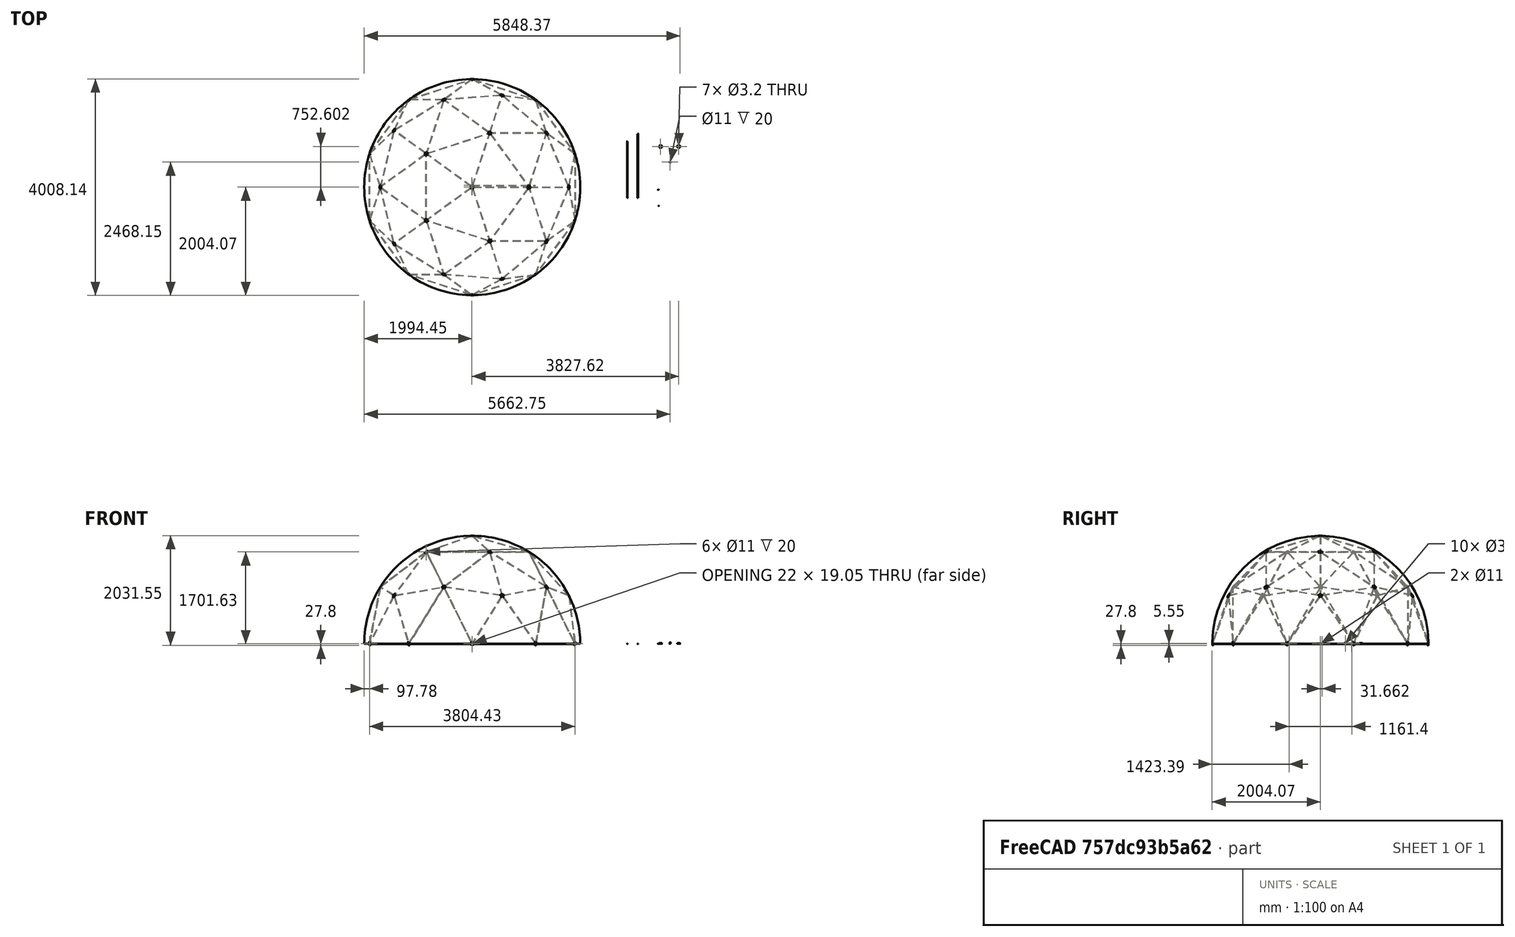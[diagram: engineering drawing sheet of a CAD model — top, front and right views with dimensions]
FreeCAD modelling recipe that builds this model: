
FCSTD DOCUMENT  (FreeCAD 0.19R24291 (Git))
Label: 02-domo-3D
License: All rights reserved
LicenseURL: http://en.wikipedia.org/wiki/All_rights_reserved
objects: Part::Feature×235, Part::Part2DObjectPython×138, App::DocumentObjectGroup×21, App::Annotation×18, Part::Mirroring×7, App::FeaturePython×4, Part::Sphere×1, Part::Cylinder×1
note: 382 computed .brp shape members not serialized (recipe doc carries the construction recipe); baked Part::Feature solids carry a one-line shape summary decoded from their .brp

FEATURE [Part::Part2DObjectPython] Line  # Draft 2D object (typed FeaturePython)
  ChamferSize = 0
  Closed = false
  End = (-1902.16,617.998,0)
  FilletRadius = 0
  Length = 1236.1
  MakeFace = true
  MapMode = 5
  Placement = pos=(-1154.86,1595.54,0) rot=(0,0,-1;0.628319rad)
  Points = (2) [(-30,6,0),(-30,-1230.1,0)]
  Start = (-1175.6,1618.02,0)
  Subdivisions = 0
FEATURE [Part::Part2DObjectPython] Line003  # Draft 2D object (typed FeaturePython)
  ChamferSize = 0
  Closed = false
  End = (-1175.6,1618.02,0)
  FilletRadius = 0
  Length = 1236.1
  MakeFace = true
  MapMode = 5
  Placement = pos=(3.56417,1969.61,0) rot=(0,0,-1;1.25664rad)
  Points = (2) [(-30,6,0),(-30,-1230.1,0)]
  Start = (3.57132e-11,2000,0)
  Subdivisions = 0
FEATURE [Part::Mirroring] Part__Mirroring  label="Line (Mirror #1)"
  Base = (0,0,0)
  Normal = (1,0,0)
  Source = -> Line
FEATURE [Part::Mirroring] Part__Mirroring001  label="Line003 (Mirror #2)"
  Base = (0,0,0)
  Normal = (1,0,0)
  Source = -> Line003
FEATURE [Part::Mirroring] Part__Mirroring002  label="Line (Mirror #3)"
  Base = (0,0,0)
  Normal = (0,1,0)
  Source = -> Line
FEATURE [Part::Mirroring] Part__Mirroring003  label="Line003 (Mirror #4)"
  Base = (0,0,0)
  Normal = (0,1,0)
  Source = -> Line003
FEATURE [Part::Mirroring] Part__Mirroring004  label="Line (Mirror #5)"
  Base = (0,0,0)
  Normal = (0,1,0)
  Source = -> Part__Mirroring
FEATURE [Part::Mirroring] Part__Mirroring005  label="Line003 (Mirror #6)"
  Base = (0,0,0)
  Normal = (0,1,0)
  Source = -> Part__Mirroring001
FEATURE [Part::Part2DObjectPython] Line006  # Draft 2D object (typed FeaturePython)
  ChamferSize = 0
  Closed = false
  End = (-1902.16,-617.998,0)
  FilletRadius = 0
  Length = 1236
  MakeFace = true
  MapMode = 5
  Points = (2) [(-1902.16,617.998,0),(-1902.16,-617.998,0)]
  Start = (-1902.16,617.998,0)
  Subdivisions = 0
FEATURE [Part::Sphere] Sphere
  Angle1 = 0
  Angle2 = 90
  Angle3 = 360
  AttacherType = Attacher::AttachEngine3D
  Radius = 2000
FEATURE [Part::Part2DObjectPython] Line014  # Draft 2D object (typed FeaturePython)
  ChamferSize = 0
  Closed = false
  End = (1902.16,3e-10,0)
  FilletRadius = 0
  Length = 1902.16
  MakeFace = true
  MapMode = 5
  Points = (2) [(-1.99975e-10,3.00133e-10,0),(1902.16,3.0025e-10,0)]
  Start = (0,0,0)
  Subdivisions = 0
FEATURE [Part::Part2DObjectPython] Line015  # Draft 2D object (typed FeaturePython)
  ChamferSize = 0
  Closed = false
  End = (1902.16,3e-10,0)
  FilletRadius = 0
  Length = 1902.16
  MakeFace = true
  MapMode = 5
  Points = (2) [(-1.99975e-10,3.00133e-10,0),(1902.16,3.0025e-10,0)]
  Start = (0,0,0)
  Subdivisions = 0
FEATURE [Part::Part2DObjectPython] Line016  # Draft 2D object (typed FeaturePython)
  ChamferSize = 0
  Closed = false
  End = (587.785,1809.02,0)
  FilletRadius = 0
  Length = 1902.11
  MakeFace = true
  MapMode = 5
  Points = (2) [(-1.99975e-10,3.00133e-10,0),(587.785,1809.02,0)]
  Start = (0,0,0)
  Subdivisions = 0
FEATURE [Part::Part2DObjectPython] Line017  # Draft 2D object (typed FeaturePython)
  ChamferSize = 0
  Closed = false
  End = (-1538.86,1118.05,0)
  FilletRadius = 0
  Length = 1902.13
  MakeFace = true
  MapMode = 5
  Points = (2) [(-1.99975e-10,3.00133e-10,0),(-1538.86,1118.05,0)]
  Start = (0,0,0)
  Subdivisions = 0
FEATURE [Part::Part2DObjectPython] Line018  # Draft 2D object (typed FeaturePython)
  ChamferSize = 0
  Closed = false
  End = (-1538.86,-1118.05,0)
  FilletRadius = 0
  Length = 1902.13
  MakeFace = true
  MapMode = 5
  Points = (2) [(-1.99975e-10,3.00133e-10,0),(-1538.86,-1118.05,0)]
  Start = (0,0,0)
  Subdivisions = 0
FEATURE [Part::Part2DObjectPython] Line019  # Draft 2D object (typed FeaturePython)
  ChamferSize = 0
  Closed = false
  End = (-577.454,-703.099,0)
  FilletRadius = 0
  Length = 1093.1
  MakeFace = true
  MapMode = 5
  Placement = pos=(1075.61,-2380.95,0) rot=(0,0,-1;0.581932rad)
  Points = (2) [(-2300,-600,0),(-2303.19,493.095,0)]
  Start = (-1175.6,-1618.02,0)
  Subdivisions = 0
FEATURE [Part::Part2DObjectPython] Line022  # Draft 2D object (typed FeaturePython)
  ChamferSize = 0
  Closed = false
  End = (587.8,-1809.01,0)
  FilletRadius = 0
  Length = 1902.11
  MakeFace = true
  MapMode = 5
  Points = (2) [(-1.99975e-10,3.00133e-10,0),(587.8,-1809.01,0)]
  Start = (0,0,0)
  Subdivisions = 0
FEATURE [Part::Part2DObjectPython] Line023  # Draft 2D object (typed FeaturePython)
  ChamferSize = 0
  Closed = false
  End = (0,0,2000)
  FilletRadius = 0
  Length = 2000
  MakeFace = true
  MapMode = 5
  Points = (2) [(-1.99975e-10,3.00133e-10,0),(1.22465e-13,-2.99952e-29,2000)]
  Start = (0,0,0)
  Subdivisions = 0
FEATURE [Part::Part2DObjectPython] DWire001  # Draft 2D object (typed FeaturePython)
  ChamferSize = 0
  Closed = true
  End = (1902.16,617.998,0)
  FilletRadius = 0
  Length = 3422.2
  MakeFace = true
  MapMode = 5
  Points = (3) [(1902.16,-617.998,0),(1788.83,-9.64734e-10,894.484),(1902.16,617.998,0)]
  Start = (1902.16,-617.998,0)
  Subdivisions = 0
FEATURE [Part::Part2DObjectPython] DWire  # Draft 2D object (typed FeaturePython)
  ChamferSize = 0
  Closed = true
  End = (587.785,1809.02,0)
  FilletRadius = 0
  Length = 6662.19
  MakeFace = true
  MapMode = 5
  Points = (3) [(1.22465e-13,0,2000),(-1.99975e-10,3.00133e-10,0),(587.785,1809.02,0)]
  Start = (0,0,2000)
  Subdivisions = 0
FEATURE [Part::Mirroring] Part__Mirroring006  label="DWire003 (Mirror #7)"
  Base = (0,0,0)
  Normal = (0,1,0)
FEATURE [Part::Part2DObjectPython] Arc  # Draft 2D object (typed FeaturePython)
  FirstAngle = 56.8247
  LastAngle = 105.817
  MakeFace = true
  MapMode = 5
  Placement = pos=(-1175.6,-1618.02,0) rot=(0,0,1;0rad)
  Radius = 1093.1
FEATURE [Part::Part2DObjectPython] Line026  # Draft 2D object (typed FeaturePython)
  ChamferSize = 0
  Closed = false
  End = (-1902.16,-617.998,0)
  FilletRadius = 0
  Length = 1093.15
  MakeFace = true
  MapMode = 5
  Points = (2) [(-809.424,-588.081,0),(-1902.16,-617.998,0)]
  Start = (-809.424,-588.081,0)
  Subdivisions = 0
FEATURE [Part::Part2DObjectPython] DWire004  # Draft 2D object (typed FeaturePython)
  ChamferSize = 0
  Closed = true
  End = (-1538.86,-1118.05,0)
  FilletRadius = 0
  Length = 6662.22
  MakeFace = true
  MapMode = 5
  Points = (3) [(1.22465e-13,0,2000),(-1.99975e-10,3.00133e-10,0),(-1538.86,-1118.05,0)]
  Start = (0,0,2000)
  Subdivisions = 0
FEATURE [Part::Part2DObjectPython] DWire005  # Draft 2D object (typed FeaturePython)
  ChamferSize = 0
  Closed = true
  End = (-1175.6,-1618.02,0)
  FilletRadius = 0
  Length = 3422.35
  MakeFace = true
  MapMode = 5
  Points = (3) [(-1902.16,-617.998,0),(-1447.19,-1051.45,894.481),(-1175.6,-1618.02,0)]
  Start = (-1902.16,-617.998,0)
  Subdivisions = 0
FEATURE [Part::Part2DObjectPython] Line027  # Draft 2D object (typed FeaturePython)
  ChamferSize = 0
  Closed = false
  End = (-878.683,234.127,0)
  FilletRadius = 0
  Length = 1093.1
  MakeFace = true
  MapMode = 5
  Placement = pos=(-2154.97,-1745.49,0) rot=(0,0,-1;1.93254rad)
  Points = (2) [(-2300,-600,0),(-2303.19,493.095,0)]
  Start = (-1902.16,617.998,0)
  Subdivisions = 0
FEATURE [Part::Part2DObjectPython] Arc003  # Draft 2D object (typed FeaturePython)
  FirstAngle = -20.5593
  LastAngle = 28.7005
  MakeFace = true
  MapMode = 5
  Placement = pos=(-1902.16,617.998,0) rot=(0,0,1;0rad)
  Radius = 1093.1
FEATURE [Part::Part2DObjectPython] DWire006  # Draft 2D object (typed FeaturePython)
  ChamferSize = 0
  Closed = true
  End = (-1538.86,1118.05,0)
  FilletRadius = 0
  Length = 6662.22
  MakeFace = true
  MapMode = 5
  Points = (3) [(1.22465e-13,0,2000),(-1.99975e-10,3.00133e-10,0),(-1538.86,1118.05,0)]
  Start = (0,0,2000)
  Subdivisions = 0
FEATURE [Part::Part2DObjectPython] DWire007  # Draft 2D object (typed FeaturePython)
  ChamferSize = 0
  Closed = true
  End = (-1902.16,617.998,0)
  FilletRadius = 0
  Length = 3422.25
  MakeFace = true
  MapMode = 5
  Points = (3) [(-1175.6,1618.02,0),(-1447.21,1051.46,894.426),(-1902.16,617.998,0)]
  Start = (-1175.6,1618.02,0)
  Subdivisions = 0
FEATURE [Part::Part2DObjectPython] DWire008  # Draft 2D object (typed FeaturePython)
  ChamferSize = 0
  Closed = true
  End = (324.937,-1000.03,1701.28)
  FilletRadius = 0
  Length = 3422.31
  MakeFace = true
  MapMode = 5
  Points = (3) [(2.23523e-10,2.82703e-10,2000),(-850.675,-618.052,1701.28),(324.937,-1000.03,1701.28)]
  Start = (2.24e-10,2.83e-10,2000)
  Subdivisions = 0
FEATURE [Part::Part2DObjectPython] DWire009  # Draft 2D object (typed FeaturePython)
  ChamferSize = 0
  Closed = true
  End = (-2e-10,3e-10,2000)
  FilletRadius = 0
  Length = 3422.3
  MakeFace = true
  MapMode = 5
  Points = (3) [(324.937,-1000.03,1701.28),(1051.49,1.3321e-09,1701.28),(-1.99876e-10,3.00061e-10,2000)]
  Start = (324.937,-1000.03,1701.28)
  Subdivisions = 0
FEATURE [Part::Part2DObjectPython] DWire010  # Draft 2D object (typed FeaturePython)
  ChamferSize = 0
  Closed = true
  End = (324.929,1000.03,1701.28)
  FilletRadius = 0
  Length = 3422.3
  MakeFace = true
  MapMode = 5
  Points = (3) [(-1.99876e-10,3.00061e-10,2000),(1051.49,1.3321e-09,1701.28),(324.929,1000.03,1701.28)]
  Start = (-2e-10,3e-10,2000)
  Subdivisions = 0
FEATURE [Part::Part2DObjectPython] DWire011  # Draft 2D object (typed FeaturePython)
  ChamferSize = 0
  Closed = true
  End = (-850.675,618.052,1701.28)
  FilletRadius = 0
  Length = 3422.3
  MakeFace = true
  MapMode = 5
  Points = (3) [(-1.99876e-10,3.00061e-10,2000),(324.929,1000.03,1701.28),(-850.675,618.052,1701.28)]
  Start = (-2e-10,3e-10,2000)
  Subdivisions = 0
FEATURE [Part::Part2DObjectPython] DWire012  # Draft 2D object (typed FeaturePython)
  ChamferSize = 0
  Closed = true
  End = (-850.675,-618.052,1701.28)
  FilletRadius = 0
  Length = 3422.3
  MakeFace = true
  MapMode = 5
  Points = (3) [(-1.99876e-10,3.00061e-10,2000),(-850.675,618.052,1701.28),(-850.675,-618.052,1701.28)]
  Start = (-2e-10,3e-10,2000)
  Subdivisions = 0
FEATURE [Part::Part2DObjectPython] Line040  # Draft 2D object (typed FeaturePython)
  ChamferSize = 0
  Closed = false
  End = (-1447.19,-1051.45,894.481)
  FilletRadius = 0
  Length = 1092.97
  MakeFace = true
  MapMode = 5
  Points = (2) [(-850.675,-618.052,1701.28),(-1447.19,-1051.45,894.481)]
  Start = (-850.675,-618.052,1701.28)
  Subdivisions = 0
FEATURE [Part::Part2DObjectPython] DWire013  # Draft 2D object (typed FeaturePython)
  ChamferSize = 0
  Closed = true
  End = (0,0,2000)
  FilletRadius = 0
  Length = 6662.22
  MakeFace = true
  MapMode = 5
  Points = (3) [(1538.88,-1118.01,0),(-1.99975e-10,3.00133e-10,0),(1.22465e-13,0,2000)]
  Start = (1538.88,-1118.01,0)
  Subdivisions = 0
FEATURE [Part::Part2DObjectPython] Arc007  # Draft 2D object (typed FeaturePython)
  FirstAngle = -90
  LastAngle = 6.05971
  MakeFace = true
  MapMode = 5
  Placement = pos=(7.36405e-11,1.01362e-10,0) rot=(0.223911,0.689153,0.689153;2.70104rad)
  Radius = 2000
  Support = -> [DWire013]
FEATURE [Part::Part2DObjectPython] DWire014  # Draft 2D object (typed FeaturePython)
  ChamferSize = 0
  Closed = true
  End = (1902.16,-617.998,0)
  FilletRadius = 0
  Length = 3708.32
  MakeFace = true
  MapMode = 5
  Points = (3) [(1175.6,-1618.02,0),(1376.39,-999.957,1051.5),(1902.16,-617.998,0)]
  Start = (1175.6,-1618.02,0)
  Subdivisions = 0
FEATURE [Part::Part2DObjectPython] DWire015  # Draft 2D object (typed FeaturePython)
  ChamferSize = 0
  Closed = true
  End = (1051.49,1.332e-09,1701.28)
  FilletRadius = 0
  Length = 3708.12
  MakeFace = true
  MapMode = 5
  Points = (3) [(1376.39,-999.957,1051.5),(324.937,-1000.03,1701.28),(1051.49,1.3321e-09,1701.28)]
  Start = (1376.39,-999.957,1051.5)
  Subdivisions = 0
FEATURE [Part::Part2DObjectPython] DWire016  # Draft 2D object (typed FeaturePython)
  ChamferSize = 0
  Closed = true
  End = (1175.6,-1618.02,0)
  FilletRadius = 0
  Length = 3422.29
  MakeFace = true
  MapMode = 5
  Points = (3) [(552.796,-1701.28,894.456),(1376.39,-999.957,1051.5),(1175.6,-1618.02,0)]
  Start = (552.796,-1701.28,894.456)
  Subdivisions = 0
FEATURE [Part::Part2DObjectPython] DWire017  # Draft 2D object (typed FeaturePython)
  ChamferSize = 0
  Closed = true
  End = (1902.16,-617.998,0)
  FilletRadius = 0
  Length = 3422.23
  MakeFace = true
  MapMode = 5
  Points = (3) [(1376.39,-999.957,1051.5),(1788.83,-9.64734e-10,894.484),(1902.16,-617.998,0)]
  Start = (1376.39,-999.957,1051.5)
  Subdivisions = 0
FEATURE [Part::Part2DObjectPython] DWire018  # Draft 2D object (typed FeaturePython)
  ChamferSize = 0
  Closed = true
  End = (1376.39,-999.957,1051.5)
  FilletRadius = 0
  Length = 3422.11
  MakeFace = true
  MapMode = 5
  Points = (3) [(324.937,-1000.03,1701.28),(552.796,-1701.28,894.456),(1376.39,-999.957,1051.5)]
  Start = (324.937,-1000.03,1701.28)
  Subdivisions = 0
FEATURE [Part::Part2DObjectPython] DWire019  # Draft 2D object (typed FeaturePython)
  ChamferSize = 0
  Closed = true
  End = (1788.83,-9.65e-10,894.484)
  FilletRadius = 0
  Length = 3421.98
  MakeFace = true
  MapMode = 5
  Points = (3) [(1376.39,-999.957,1051.5),(1051.49,1.3321e-09,1701.28),(1788.83,-9.64734e-10,894.484)]
  Start = (1376.39,-999.957,1051.5)
  Subdivisions = 0
FEATURE [Part::Part2DObjectPython] DWire020  # Draft 2D object (typed FeaturePython)
  ChamferSize = 0
  Closed = true
  End = (1175.6,1618.02,0)
  FilletRadius = 0
  Length = 3708.32
  MakeFace = true
  MapMode = 5
  Points = (3) [(1902.16,617.998,0),(1376.39,999.957,1051.5),(1175.6,1618.02,0)]
  Start = (1902.16,617.998,0)
  Subdivisions = 0
FEATURE [Part::Part2DObjectPython] DWire021  # Draft 2D object (typed FeaturePython)
  ChamferSize = 0
  Closed = true
  End = (-1175.6,1618.02,0)
  FilletRadius = 0
  Length = 3708.32
  MakeFace = true
  MapMode = 5
  Points = (3) [(-525.738,1618.01,1051.5),(3.56977e-11,2000,0),(-1175.6,1618.02,0)]
  Start = (-525.738,1618.01,1051.5)
  Subdivisions = 0
FEATURE [Part::Part2DObjectPython] DWire022  # Draft 2D object (typed FeaturePython)
  ChamferSize = 0
  Closed = true
  End = (-1902.16,-617.998,0)
  FilletRadius = 0
  Length = 3708.18
  MakeFace = true
  MapMode = 5
  Points = (3) [(-1701.28,-1.02242e-09,1051.5),(-1902.16,617.998,0),(-1902.16,-617.998,0)]
  Start = (-1701.28,-1.022e-09,1051.5)
  Subdivisions = 0
FEATURE [Part::Part2DObjectPython] DWire023  # Draft 2D object (typed FeaturePython)
  ChamferSize = 0
  Closed = true
  End = (-3.6e-11,-2000,0)
  FilletRadius = 0
  Length = 3708.32
  MakeFace = true
  MapMode = 5
  Points = (3) [(-525.738,-1618.01,1051.5),(-1175.6,-1618.02,0),(-3.5925e-11,-2000,0)]
  Start = (-525.738,-1618.01,1051.5)
  Subdivisions = 0
FEATURE [Part::Part2DObjectPython] DWire024  # Draft 2D object (typed FeaturePython)
  ChamferSize = 0
  Closed = true
  End = (324.929,1000.03,1701.28)
  FilletRadius = 0
  Length = 3708.14
  MakeFace = true
  MapMode = 5
  Points = (3) [(1051.49,1.3321e-09,1701.28),(1376.39,999.957,1051.5),(324.929,1000.03,1701.28)]
  Start = (1051.49,1.332e-09,1701.28)
  Subdivisions = 0
FEATURE [Part::Part2DObjectPython] DWire025  # Draft 2D object (typed FeaturePython)
  ChamferSize = 0
  Closed = true
  End = (1376.39,999.957,1051.5)
  FilletRadius = 0
  Length = 3421.98
  MakeFace = true
  MapMode = 5
  Points = (3) [(1051.49,1.3321e-09,1701.28),(1788.83,-9.64734e-10,894.484),(1376.39,999.957,1051.5)]
  Start = (1051.49,1.332e-09,1701.28)
  Subdivisions = 0
FEATURE [Part::Part2DObjectPython] DWire026  # Draft 2D object (typed FeaturePython)
  ChamferSize = 0
  Closed = true
  End = (1376.39,999.957,1051.5)
  FilletRadius = 0
  Length = 3422.23
  MakeFace = true
  MapMode = 5
  Points = (3) [(1788.83,-9.64734e-10,894.484),(1902.16,617.998,0),(1376.39,999.957,1051.5)]
  Start = (1788.83,-9.65e-10,894.484)
  Subdivisions = 0
FEATURE [Part::Part2DObjectPython] DWire027  # Draft 2D object (typed FeaturePython)
  ChamferSize = 0
  Closed = true
  End = (552.796,1701.28,894.456)
  FilletRadius = 0
  Length = 3422.29
  MakeFace = true
  MapMode = 5
  Points = (3) [(1376.39,999.957,1051.5),(1175.6,1618.02,0),(552.796,1701.28,894.456)]
  Start = (1376.39,999.957,1051.5)
  Subdivisions = 0
FEATURE [Part::Part2DObjectPython] DWire028  # Draft 2D object (typed FeaturePython)
  ChamferSize = 0
  Closed = true
  End = (552.796,1701.28,894.456)
  FilletRadius = 0
  Length = 3422.12
  MakeFace = true
  MapMode = 5
  Points = (3) [(324.929,1000.03,1701.28),(1376.39,999.957,1051.5),(552.796,1701.28,894.456)]
  Start = (324.929,1000.03,1701.28)
  Subdivisions = 0
FEATURE [Part::Part2DObjectPython] DWire029  # Draft 2D object (typed FeaturePython)
  ChamferSize = 0
  Closed = true
  End = (-3.6e-11,2000,0)
  FilletRadius = 0
  Length = 3422.29
  MakeFace = true
  MapMode = 5
  Points = (3) [(-525.738,1618.01,1051.5),(552.796,1701.28,894.456),(-3.5925e-11,2000,0)]
  Start = (-525.738,1618.01,1051.5)
  Subdivisions = 0
FEATURE [Part::Part2DObjectPython] DWire030  # Draft 2D object (typed FeaturePython)
  ChamferSize = 0
  Closed = true
  End = (-525.738,1618.01,1051.5)
  FilletRadius = 0
  Length = 3422.11
  MakeFace = true
  MapMode = 5
  Points = (3) [(324.929,1000.03,1701.28),(552.796,1701.28,894.456),(-525.738,1618.01,1051.5)]
  Start = (324.929,1000.03,1701.28)
  Subdivisions = 0
FEATURE [Part::Part2DObjectPython] DWire031  # Draft 2D object (typed FeaturePython)
  ChamferSize = 0
  Closed = true
  End = (-850.675,618.052,1701.28)
  FilletRadius = 0
  Length = 3708.14
  MakeFace = true
  MapMode = 5
  Points = (3) [(324.929,1000.03,1701.28),(-525.738,1618.01,1051.5),(-850.675,618.052,1701.28)]
  Start = (324.929,1000.03,1701.28)
  Subdivisions = 0
FEATURE [Part::Part2DObjectPython] DWire032  # Draft 2D object (typed FeaturePython)
  ChamferSize = 0
  Closed = true
  End = (-1447.21,1051.46,894.426)
  FilletRadius = 0
  Length = 3422.21
  MakeFace = true
  MapMode = 5
  Points = (3) [(-525.738,1618.01,1051.5),(-1175.6,1618.02,0),(-1447.21,1051.46,894.426)]
  Start = (-525.738,1618.01,1051.5)
  Subdivisions = 0
FEATURE [Part::Part2DObjectPython] DWire033  # Draft 2D object (typed FeaturePython)
  ChamferSize = 0
  Closed = true
  End = (-1447.21,1051.46,894.426)
  FilletRadius = 0
  Length = 3422.1
  MakeFace = true
  MapMode = 5
  Points = (3) [(-525.738,1618.01,1051.5),(-850.675,618.052,1701.28),(-1447.21,1051.46,894.426)]
  Start = (-525.738,1618.01,1051.5)
  Subdivisions = 0
FEATURE [Part::Part2DObjectPython] DWire034  # Draft 2D object (typed FeaturePython)
  ChamferSize = 0
  Closed = true
  End = (-1701.28,-1.022e-09,1051.5)
  FilletRadius = 0
  Length = 3422.12
  MakeFace = true
  MapMode = 5
  Points = (3) [(-850.675,618.052,1701.28),(-1447.21,1051.46,894.426),(-1701.28,-1.02242e-09,1051.5)]
  Start = (-850.675,618.052,1701.28)
  Subdivisions = 0
FEATURE [Part::Part2DObjectPython] DWire035  # Draft 2D object (typed FeaturePython)
  ChamferSize = 0
  Closed = true
  End = (-1701.28,-1.022e-09,1051.5)
  FilletRadius = 0
  Length = 3422.26
  MakeFace = true
  MapMode = 5
  Points = (3) [(-1447.21,1051.46,894.426),(-1902.16,617.998,0),(-1701.28,-1.02242e-09,1051.5)]
  Start = (-1447.21,1051.46,894.426)
  Subdivisions = 0
FEATURE [Part::Part2DObjectPython] DWire036  # Draft 2D object (typed FeaturePython)
  ChamferSize = 0
  Closed = true
  End = (-850.675,-618.052,1701.28)
  FilletRadius = 0
  Length = 3708.14
  MakeFace = true
  MapMode = 5
  Points = (3) [(-850.675,618.052,1701.28),(-1701.28,-1.02242e-09,1051.5),(-850.675,-618.052,1701.28)]
  Start = (-850.675,618.052,1701.28)
  Subdivisions = 0
FEATURE [Part::Part2DObjectPython] DWire037  # Draft 2D object (typed FeaturePython)
  ChamferSize = 0
  Closed = true
  End = (-1447.19,-1051.45,894.481)
  FilletRadius = 0
  Length = 3422.04
  MakeFace = true
  MapMode = 5
  Points = (3) [(-1701.28,-1.02242e-09,1051.5),(-850.675,-618.052,1701.28),(-1447.19,-1051.45,894.481)]
  Start = (-1701.28,-1.022e-09,1051.5)
  Subdivisions = 0
FEATURE [Part::Part2DObjectPython] DWire038  # Draft 2D object (typed FeaturePython)
  ChamferSize = 0
  Closed = true
  End = (-1447.19,-1051.45,894.481)
  FilletRadius = 0
  Length = 3422.29
  MakeFace = true
  MapMode = 5
  Points = (3) [(-1701.28,-1.02242e-09,1051.5),(-1902.16,-617.998,0),(-1447.19,-1051.45,894.481)]
  Start = (-1701.28,-1.022e-09,1051.5)
  Subdivisions = 0
FEATURE [Part::Part2DObjectPython] DWire039  # Draft 2D object (typed FeaturePython)
  ChamferSize = 0
  Closed = true
  End = (-525.738,-1618.01,1051.5)
  FilletRadius = 0
  Length = 3422.02
  MakeFace = true
  MapMode = 5
  Points = (3) [(-850.675,-618.052,1701.28),(-1447.19,-1051.45,894.481),(-525.738,-1618.01,1051.5)]
  Start = (-850.675,-618.052,1701.28)
  Subdivisions = 0
FEATURE [Part::Part2DObjectPython] DWire040  # Draft 2D object (typed FeaturePython)
  ChamferSize = 0
  Closed = true
  End = (324.937,-1000.03,1701.28)
  FilletRadius = 0
  Length = 3708.15
  MakeFace = true
  MapMode = 5
  Points = (3) [(-850.675,-618.052,1701.28),(-525.738,-1618.01,1051.5),(324.937,-1000.03,1701.28)]
  Start = (-850.675,-618.052,1701.28)
  Subdivisions = 0
FEATURE [Part::Part2DObjectPython] DWire041  # Draft 2D object (typed FeaturePython)
  ChamferSize = 0
  Closed = true
  End = (-1447.19,-1051.45,894.481)
  FilletRadius = 0
  Length = 3422.24
  MakeFace = true
  MapMode = 5
  Points = (3) [(-525.738,-1618.01,1051.5),(-1175.6,-1618.02,0),(-1447.19,-1051.45,894.481)]
  Start = (-525.738,-1618.01,1051.5)
  Subdivisions = 0
FEATURE [Part::Part2DObjectPython] DWire042  # Draft 2D object (typed FeaturePython)
  ChamferSize = 0
  Closed = true
  End = (552.796,-1701.28,894.456)
  FilletRadius = 0
  Length = 3422.12
  MakeFace = true
  MapMode = 5
  Points = (3) [(-525.738,-1618.01,1051.5),(324.937,-1000.03,1701.28),(552.796,-1701.28,894.456)]
  Start = (-525.738,-1618.01,1051.5)
  Subdivisions = 0
FEATURE [Part::Part2DObjectPython] DWire043  # Draft 2D object (typed FeaturePython)
  ChamferSize = 0
  Closed = true
  End = (552.796,-1701.28,894.456)
  FilletRadius = 0
  Length = 3422.29
  MakeFace = true
  MapMode = 5
  Points = (3) [(-525.738,-1618.01,1051.5),(-3.5925e-11,-2000,0),(552.796,-1701.28,894.456)]
  Start = (-525.738,-1618.01,1051.5)
  Subdivisions = 0
FEATURE [App::DocumentObjectGroup] Group001  label="Top-pentagon"
  Group = -> [DWire010,DWire011,DWire012,DWire008,DWire009]
FEATURE [App::DocumentObjectGroup] Group002  label="Pentagon-1"
  Group = -> [DWire019,DWire025,DWire026,DWire001,DWire017]
FEATURE [App::DocumentObjectGroup] Group003  label="Pentagon-2"
  Group = -> [DWire028,DWire030,DWire029,Part__Mirroring006,DWire027]
FEATURE [App::DocumentObjectGroup] Group004  label="Pentagon-3"
  Group = -> [DWire033,DWire034,DWire035,DWire007,DWire032]
FEATURE [App::DocumentObjectGroup] Group005  label="Pentagon-4"
  Group = -> [DWire037,DWire038,DWire005,DWire041,Line040,DWire039]
FEATURE [Part::Part2DObjectPython] DWire044  # Draft 2D object (typed FeaturePython)
  ChamferSize = 0
  Closed = true
  End = (1175.6,-1618.02,0)
  FilletRadius = 0
  Length = 3422.3
  MakeFace = true
  MapMode = 5
  Points = (3) [(-3.5925e-11,-2000,0),(552.796,-1701.28,894.456),(1175.6,-1618.02,0)]
  Start = (-3.6e-11,-2000,0)
  Subdivisions = 0
FEATURE [App::DocumentObjectGroup] Group006  label="Pentagon-5"
  Group = -> [DWire042,DWire043,DWire016,DWire018,DWire044]
FEATURE [App::DocumentObjectGroup] Group007  label="Aux"
  Group = -> [Part__Mirroring002,Part__Mirroring003,Part__Mirroring004,Part__Mirroring005,Line006,Line014,Line015,Line016,Line017,Line018,Line019,Line022,Line023,DWire,Arc,Line026,DWire004,Line027,Arc003,DWire006,DWire013,Arc007,Sphere]
FEATURE [Part::Part2DObjectPython] DWire045  label="Bottom"  # Draft 2D object (typed FeaturePython)
  ChamferSize = 0
  Closed = true
  End = (1902.16,-617.998,0)
  FilletRadius = 0
  Length = 12360.8
  MakeFace = true
  MapMode = 5
  Points = (10) [(1902.16,617.998,0),(1175.6,1618.02,0),(3.56977e-11,2000,0),(-1175.6,1618.02,0),(-1902.16,617.998,0),(-1902.16,-617.998,0),(-1175.6,-1618.02,0),+3 more]
  Start = (1902.16,617.998,0)
  Subdivisions = 0
FEATURE [App::DocumentObjectGroup] Group008  label="Green-triangles"
  Group = -> [DWire023,DWire040,DWire015,DWire014,DWire024,DWire031,DWire036,DWire022,DWire021,DWire020]
FEATURE [Part::Feature] Clone002  label="Hub-007"
  Placement = pos=(1044.95,2.82704e-10,1690.69) rot=(0.191324,0.71403,0.673466;0.757331rad)
  shape: bbox 49.68 x 55.6 x 37.22 mm, 28 faces (baked)
FEATURE [Part::Feature] Clone005  label="strutcap004"
  Placement = pos=(1066.92,2.82878e-10,1684.4) rot=(0.932253,0,0.361806;3.14159rad)
  shape: bbox 31.1 x 20 x 29.82 mm, 19 faces (baked)
FEATURE [Part::Feature] Clone008  label="strutcap007"
  Placement = pos=(1038.85,-19.0526,1701.75) rot=(0.667656,-0.64473,0.372235;1.42598rad)
  shape: bbox 25.29 x 31.07 x 25.73 mm, 19 faces (baked)
FEATURE [Part::Feature] Clone009  label="strutcap008"
  Placement = pos=(1029.49,2.82532e-10,1707.53) rot=(0,-1,0;1.294rad)
  shape: bbox 31.29 x 20 x 25.37 mm, 19 faces (baked)
FEATURE [Part::Feature] Clone028  label="strutcap025"
  Placement = pos=(1902.2,-594.877,0) rot=(-1,-1.4e-05,1.4e-05;1.5708rad)
  shape: bbox 20.3 x 30 x 20 mm, 19 faces (baked)
FEATURE [Part::Feature] Clone030  label="strutcap027"
  Placement = pos=(1888.76,-636.496,-2.5e-14) rot=(0.909046,-0.294649,-0.294649;1.66601rad)
  shape: bbox 27.81 x 32.24 x 20 mm, 19 faces (baked)
FEATURE [Part::Feature] Clone031  label="Hub-012"
  Placement = pos=(1889.5,-613.884,-5e-15) rot=(0.154555,0.97582,-0.154555;1.59527rad)
  shape: bbox 27.47 x 52.09 x 55.6 mm, 28 faces (baked)
FEATURE [Part::Feature] Cylinder014  label="Varilla-B-modif-003"
  Placement = pos=(1902.16,593.953,-2.89e-13) rot=(1,1.4e-05,1.4e-05;1.5708rad)
  shape: bbox 10.03 x 1189 x 10 mm, 3 faces (baked)
FEATURE [App::DocumentObjectGroup] Group012
FEATURE [App::DocumentObjectGroup] Group  label="Domo-superficies"
  Group = -> [Group001,Group002,Group003,Group004,Group005,Group006,Group008,DWire045,Group012]
FEATURE [Part::Feature] Clone001004  label="Hub5-01-clave002"
  Placement = pos=(-1.81309e-05,2.82703e-10,1987.55) rot=(0,0,-1;0.314151rad)
  shape: bbox 54.38 x 55.6 x 12.4 mm, 25 faces (baked)
FEATURE [Part::Feature] Clone  label="strutcap031"
  Placement = pos=(22.0001,2.82694e-10,1993.75) rot=(0.797896,0,0.602796;3.14159rad)
  shape: bbox 32.05 x 20 x 22.68 mm, 19 faces (baked)
FEATURE [Part::Feature] Clone001005  label="Hub5-01-clave003"
  Placement = pos=(1777.69,2.82703e-10,888.915) rot=(0.523905,0.082976,0.847726;2.87466rad)
  shape: bbox 33.84 x 55.6 x 51.33 mm, 25 faces (baked)
FEATURE [Part::Feature] Clone001006  label="strutcap032"
  Placement = pos=(1773.4,2.82716e-10,911.365) rot=(0,-1,0;0.740475rad)
  shape: bbox 29.03 x 20 x 31.71 mm, 19 faces (baked)
FEATURE [Part::Feature] Clone001007  label="Hub-014"
  Placement = pos=(1889.5,613.885,-5e-15) rot=(-0.154531,0.975828,0.154531;1.59526rad)
  shape: bbox 27.47 x 52.09 x 55.6 mm, 28 faces (baked)
FEATURE [Part::Feature] Clone001008  label="strutcap033"
  Placement = pos=(1902.19,595.158,-2.5e-14) rot=(1,0.00069,0.00069;1.5708rad)
  shape: bbox 20.33 x 30.01 x 20 mm, 19 faces (baked)
FEATURE [Part::Feature] Clone001009  label="strutcap034"
  Placement = pos=(1888.6,636.724,0) rot=(-0.908667,-0.295233,0.295233;1.66643rad)
  shape: bbox 27.82 x 32.23 x 20 mm, 19 faces (baked)
FEATURE [Part::Feature] Clone001010  label="strutcap035"
  Placement = pos=(1899.8,-604.923,18.9221) rot=(-0.98127,-0.136231,0.136202;0.618302rad)
  shape: bbox 20 x 28.03 x 30.96 mm, 19 faces (baked)
FEATURE [Part::Feature] Clone001012  label="strutcap037"
  Placement = pos=(1791.2,-12.9311,875.769) rot=(0.998074,0.043631,0.044104;2.5353rad)
  shape: bbox 22.47 x 27.49 x 30.68 mm, 19 faces (baked)
FEATURE [Part::Cylinder] Cylinder015  label="Cylinder084"
  Angle = 360
  AttacherType = Attacher::AttachEngine3D
  Height = 1047.11
  Placement = pos=(1066.92,2.82853e-10,1684.4) rot=(0.681894,-0.681894,0.264655;3.65904rad)
  Radius = 5
FEATURE [Part::Feature] Cylinder016  label="Cylinder001"
  Placement = pos=(1791.23,-12.9283,875.771) rot=(0.998113,0.043415,0.043415;2.53525rad)
  shape: bbox 118.5 x 600.2 x 862.6 mm, 3 faces (baked)
FEATURE [Part::Feature] Clone001013  label="strutcap038"
  Placement = pos=(1791.12,13.8918,876.408) rot=(0.993179,0.082001,0.082896;3.73273rad)
  shape: bbox 22.73 x 28.03 x 30.67 mm, 19 faces (baked)
FEATURE [Part::Feature] Cylinder017  label="Cylinder002"
  Placement = pos=(1791.15,13.8946,876.414) rot=(0.993219,0.08221,0.08221;3.73262rad)
  shape: bbox 118.5 x 600.7 x 862.3 mm, 3 faces (baked)
FEATURE [Part::Feature] Clone001014  label="strutcap039"
  Placement = pos=(1899.68,606.357,19.8831) rot=(0.934186,-0.252314,0.25226;0.634069rad)
  shape: bbox 20 x 27.5 x 31.62 mm, 19 faces (baked)
FEATURE [Part::Feature] Cylinder018  label="Cylinder003"
  Placement = pos=(22.0001,2.82669e-10,1993.75) rot=(-0.623692,0.623692,-0.471188;2.26093rad)
  shape: bbox 1010 x 10 x 295.8 mm, 3 faces (baked)
FEATURE [Part::Feature] Cylinder019  label="Cylinder004"
  Placement = pos=(6.79821,20.9234,1993.75) rot=(-0.980863,0.155349,-0.117363;1.86613rad)
  shape: bbox 320.8 x 962 x 295.8 mm, 3 faces (baked)
FEATURE [Part::Feature] Clone001015  label="strutcap040"
  Placement = pos=(6.79821,20.9234,1993.75) rot=(0.690291,0.501531,0.521503;3.86596rad)
  shape: bbox 23.54 x 32.47 x 22.68 mm, 19 faces (baked)
FEATURE [Part::Feature] Clone001016  label="strutcap041"
  Placement = pos=(318.122,979.108,1707.53) rot=(0.463915,-0.638519,0.614065;1.73821rad)
  shape: bbox 23.11 x 31.33 x 25.37 mm, 19 faces (baked)
FEATURE [Part::Feature] Clone001018  label="Hub-015"
  Placement = pos=(322.898,993.806,1690.69) rot=(-0.123041,0.320528,0.939214;1.84115rad)
  shape: bbox 55.11 x 51.63 x 37.22 mm, 28 faces (baked)
FEATURE [Part::Feature] Clone001020  label="strutcap044"
  Placement = pos=(339.134,982.12,1701.75) rot=(0.773329,-0.182879,0.607056;2.21695rad)
  shape: bbox 29.76 x 30.45 x 20.75 mm, 19 faces (baked)
FEATURE [Part::Feature] Clone007  label="strutcap006"
  Placement = pos=(1038.85,19.0526,1701.75) rot=(-0.64113,-0.730539,-0.235086;1.6431rad)
  shape: bbox 27.52 x 31.98 x 20.74 mm, 19 faces (baked)
FEATURE [Part::Feature] Cylinder020  label="Varilla-B-modif-004"
  Placement = pos=(340.068,980.833,1701.75) rot=(0.90866,0.295244,0.295244;1.66644rad)
  shape: bbox 706.9 x 967.7 x 10 mm, 3 faces (baked)
FEATURE [Part::Feature] Clone001023  label="Hub-016"
  Placement = pos=(1367.83,993.738,1044.94) rot=(0.480375,0.156077,0.863064;3.68838rad)
  shape: bbox 46.36 x 51.63 x 50.11 mm, 28 faces (baked)
FEATURE [Part::Feature] Clone001027  label="strutcap049"
  Placement = pos=(1385.02,979.037,1048.2) rot=(0.929901,-0.068235,0.361425;1.8922rad)
  shape: bbox 27.6 x 31.33 x 20.3 mm, 19 faces (baked)
FEATURE [Part::Feature] Clone001030  label="strutcap052"
  Placement = pos=(1779.91,20.6545,898.82) rot=(-0.909103,-0.414228,-0.044114;1.42856rad)
  shape: bbox 24.46 x 32.53 x 22.38 mm, 19 faces (baked)
FEATURE [Part::Feature] Cylinder021  label="Cylinder005"
  Placement = pos=(1779.94,20.6643,898.834) rot=(-0.908834,-0.414887,-0.043473;1.42913rad)
  shape: bbox 403.8 x 962.4 x 159.4 mm, 3 faces (baked)
FEATURE [Part::Feature] Clone001031  label="strutcap053"
  Placement = pos=(1780.84,-21.3342,896.949) rot=(0.871498,-0.474485,0.123916;1.43836rad)
  shape: bbox 24.48 x 32.39 x 22.88 mm, 19 faces (baked)
FEATURE [Part::Feature] Cylinder022  label="Cylinder006"
  Placement = pos=(1780.87,-21.342,896.969) rot=(0.871257,-0.475095,0.123269;1.43902rad)
  shape: bbox 404.7 x 961.7 x 161.3 mm, 3 faces (baked)
FEATURE [Part::Feature] Clone001032  label="strutcap054"
  Placement = pos=(1385.02,-979.035,1048.21) rot=(-0.930319,-0.067054,-0.360569;1.89034rad)
  shape: bbox 27.6 x 31.33 x 20.29 mm, 19 faces (baked)
FEATURE [Part::Feature] Clone001033  label="Hub-017"
  Placement = pos=(1367.82,-993.731,1044.96) rot=(0.270395,0.832171,-0.484126;1.1821rad)
  shape: bbox 46.31 x 51.62 x 50.16 mm, 28 faces (baked)
FEATURE [Part::Feature] Clone001036  label="strutcap057"
  Placement = pos=(1359.16,-1014.63,1048.21) rot=(0.830217,-0.556143,-0.038018;1.57228rad)
  shape: bbox 27.82 x 32.54 x 20 mm, 19 faces (baked)
FEATURE [Part::Feature] Clone001037  label="strutcap058"
  Placement = pos=(1373.71,-1011.61,1031.99) rot=(0.909326,-0.37369,0.182983;2.49398rad)
  shape: bbox 21.91 x 31.15 x 29.81 mm, 19 faces (baked)
FEATURE [Part::Feature] Clone001038  label="strutcap059"
  Placement = pos=(1386.64,-993.808,1031.99) rot=(0.962095,-0.192679,0.192997;3.57034rad)
  shape: bbox 28.43 x 23.66 x 30.86 mm, 19 faces (baked)
FEATURE [Part::Part2DObjectPython] Line054  # Draft 2D object (typed FeaturePython)
  ChamferSize = 0
  Closed = false
  End = (1902.16,-617.998,0)
  FilletRadius = 0
  Length = 1236.1
  MakeFace = true
  MapMode = 5
  Points = (2) [(1175.6,-1618.02,0),(1902.16,-617.998,0)]
  Start = (1175.6,-1618.02,0)
  Subdivisions = 0
FEATURE [Part::Part2DObjectPython] Line055  # Draft 2D object (typed FeaturePython)
  ChamferSize = 0
  Closed = false
  End = (1902.16,617.998,0)
  FilletRadius = 0
  Length = 1236
  MakeFace = true
  MapMode = 5
  Points = (2) [(1902.16,-617.998,0),(1902.16,617.998,0)]
  Start = (1902.16,-617.998,0)
  Subdivisions = 0
FEATURE [Part::Part2DObjectPython] Line056  # Draft 2D object (typed FeaturePython)
  ChamferSize = 0
  Closed = false
  End = (1376.39,-999.957,1051.5)
  FilletRadius = 0
  Length = 1236
  MakeFace = true
  MapMode = 5
  Points = (2) [(1051.49,1.3321e-09,1701.28),(1376.39,-999.957,1051.5)]
  Start = (1051.49,1.332e-09,1701.28)
  Subdivisions = 0
FEATURE [Part::Part2DObjectPython] Line057  # Draft 2D object (typed FeaturePython)
  ChamferSize = 0
  Closed = false
  End = (1902.16,-617.998,0)
  FilletRadius = 0
  Length = 1236.11
  MakeFace = true
  MapMode = 5
  Points = (2) [(1376.39,-999.957,1051.5),(1902.16,-617.998,0)]
  Start = (1376.39,-999.957,1051.5)
  Subdivisions = 0
FEATURE [Part::Part2DObjectPython] Line058  # Draft 2D object (typed FeaturePython)
  ChamferSize = 0
  Closed = false
  End = (1376.39,999.957,1051.5)
  FilletRadius = 0
  Length = 1236
  MakeFace = true
  MapMode = 5
  Points = (2) [(1051.49,1.3321e-09,1701.28),(1376.39,999.957,1051.5)]
  Start = (1051.49,1.332e-09,1701.28)
  Subdivisions = 0
FEATURE [Part::Part2DObjectPython] Line059  # Draft 2D object (typed FeaturePython)
  ChamferSize = 0
  Closed = false
  End = (1902.16,617.998,0)
  FilletRadius = 0
  Length = 1236.11
  MakeFace = true
  MapMode = 5
  Points = (2) [(1376.39,999.957,1051.5),(1902.16,617.998,0)]
  Start = (1376.39,999.957,1051.5)
  Subdivisions = 0
FEATURE [Part::Feature] Cylinder023  label="Varilla-B-modif-005"
  Placement = pos=(1891.94,625.428,20.4541) rot=(-0.256517,-0.683428,-0.683465;0.767356rad)
  shape: bbox 514.7 x 376.8 x 1017 mm, 3 faces (baked)
FEATURE [Part::Feature] Clone001039  label="strutcap060"
  Placement = pos=(1386.87,993.248,1032.31) rot=(0.963511,0.189033,0.189506;2.73838rad)
  shape: bbox 28.28 x 23.32 x 30.96 mm, 19 faces (baked)
FEATURE [Part::Feature] Clone001040  label="strutcap061"
  Placement = pos=(1892,626.262,19.0526) rot=(-0.586671,-0.615427,0.526371;0.557536rad)
  shape: bbox 24.41 x 24.08 x 32.46 mm, 19 faces (baked)
FEATURE [Part::Feature] Clone001041  label="strutcap062"
  Placement = pos=(1370.43,982.035,1064.4) rot=(0.652966,-0.542424,0.528594;1.20781rad)
  shape: bbox 22.88 x 30.45 x 29.86 mm, 19 faces (baked)
FEATURE [Part::Feature] Cylinder024  label="Varilla-B-modif-006"
  Placement = pos=(1057.35,20.059,1689.56) rot=(0.887762,0.32548,0.325486;3.92675rad)
  shape: bbox 322.6 x 967 x 634.3 mm, 3 faces (baked)
FEATURE [Part::Feature] Clone001042  label="strutcap063"
  Placement = pos=(1057.34,19.1988,1690.32) rot=(0.882765,0.34052,0.323687;3.95983rad)
  shape: bbox 24.7 x 32.04 x 26.61 mm, 19 faces (baked)
FEATURE [Part::Feature] Cylinder025  label="Varilla-B-modif-007"
  Placement = pos=(1386.68,-992.502,1030.9) rot=(0.93165,0.256925,0.256939;3.33301rad)
  shape: bbox 514.9 x 375.8 x 1017 mm, 3 faces (baked)
FEATURE [Part::Feature] Clone001043  label="strutcap064"
  Placement = pos=(1892.07,-626.034,19.189) rot=(0.64134,-0.542546,-0.542518;0.709896rad)
  shape: bbox 25.5 x 26.02 x 32.03 mm, 19 faces (baked)
FEATURE [Part::Feature] Clone001044  label="strutcap065"
  Placement = pos=(1370.47,-982.061,1064.43) rot=(-0.67332,-0.525087,-0.520503;1.20241rad)
  shape: bbox 22.54 x 30.53 x 29.82 mm, 19 faces (baked)
FEATURE [Part::Feature] Clone001045  label="strutcap066"
  Placement = pos=(1057.56,-19.0526,1690.18) rot=(0.887841,-0.325204,0.325548;2.35642rad)
  shape: bbox 25.29 x 31.82 x 26.9 mm, 19 faces (baked)
FEATURE [Part::Feature] Cylinder027  label="Varilla-B-modif-009"
  Placement = pos=(1370.47,-982.061,1064.43) rot=(-0.669151,-0.525446,-0.525494;1.2188rad)
  shape: bbox 322.1 x 967.7 x 633.5 mm, 3 faces (baked)
FEATURE [Part::Part2DObjectPython] Line060  # Draft 2D object (typed FeaturePython)
  ChamferSize = 0
  Closed = false
  End = (324.929,1000.03,1701.28)
  FilletRadius = 0
  Length = 1236.1
  MakeFace = true
  MapMode = 5
  Points = (2) [(-850.675,618.052,1701.28),(324.929,1000.03,1701.28)]
  Start = (-850.675,618.052,1701.28)
  Subdivisions = 0
FEATURE [Part::Feature] Clone001047  label="strutcap068"
  Placement = pos=(302.894,993.894,1701.75) rot=(-0.095426,-0.931982,0.349719;1.72702rad)
  shape: bbox 31.97 x 22.84 x 20.72 mm, 19 faces (baked)
FEATURE [Part::Feature] Clone001049  label="strutcap070"
  Placement = pos=(-17.7986,12.9312,1993.75) rot=(-0.300922,-0.926155,-0.227341;1.92055rad)
  shape: bbox 31.35 x 28.31 x 22.68 mm, 19 faces (baked)
FEATURE [Part::Feature] Cylinder  label="Cylinder007"
  Placement = pos=(-17.7986,12.9312,1993.75) rot=(-0.842809,-0.429437,0.324432;2.00762rad)
  shape: bbox 821.2 x 600.3 x 295.8 mm, 3 faces (baked)
FEATURE [Part::Feature] Clone001050  label="Hub-018"
  Placement = pos=(-845.385,614.197,1690.69) rot=(-0.229479,0.149024,0.961837;3.04087rad)
  shape: bbox 52.89 x 52.48 x 37.22 mm, 28 faces (baked)
FEATURE [Part::Feature] Clone001051  label="strutcap071"
  Placement = pos=(-832.882,605.113,1707.53) rot=(0.591556,-0.192206,0.783019;2.64333rad)
  shape: bbox 30.27 x 27.49 x 25.37 mm, 19 faces (baked)
FEATURE [Part::Feature] Clone001052  label="strutcap072"
  Placement = pos=(-829.253,626.027,1701.75) rot=(0.656731,0.274649,0.702334;3.0586rad)
  shape: bbox 31.36 x 25.66 x 20.75 mm, 19 faces (baked)
FEATURE [Part::Feature] Clone001053  label="strutcap073"
  Placement = pos=(-844.393,637.027,1690.18) rot=(0.558841,0.681764,0.472117;3.47389rad)
  shape: bbox 22.99 x 32.33 x 26.68 mm, 19 faces (baked)
FEATURE [Part::Feature] Clone001054  label="strutcap074"
  Placement = pos=(-863.162,627.113,1684.4) rot=(0.306814,0.944291,0.119074;3.84415rad)
  shape: bbox 29.74 x 26.84 x 29.82 mm, 19 faces (baked)
FEATURE [Part::Feature] Clone001055  label="strutcap075"
  Placement = pos=(-866.791,606.199,1690.18) rot=(-0.037385,0.949845,-0.310478;3.97036rad)
  shape: bbox 31.57 x 26.83 x 26.72 mm, 19 faces (baked)
FEATURE [Part::Feature] Clone001056  label="strutcap076"
  Placement = pos=(-851.651,595.199,1701.75) rot=(-0.384951,0.662639,-0.642435;3.89838rad)
  shape: bbox 20.26 x 30.22 x 20.72 mm, 19 faces (baked)
FEATURE [Part::Feature] Cylinder028  label="Varilla-B-modif-010"
  Placement = pos=(-827.741,626.518,1701.75) rot=(0.456965,0.628961,0.628961;2.28433rad)
  shape: bbox 1134 x 376.9 x 10 mm, 3 faces (baked)
FEATURE [Part::Part2DObjectPython] Line061  # Draft 2D object (typed FeaturePython)
  ChamferSize = 0
  Closed = false
  End = (-850.675,-618.052,1701.28)
  FilletRadius = 0
  Length = 1236.1
  MakeFace = true
  MapMode = 5
  Points = (2) [(-850.675,618.052,1701.28),(-850.675,-618.052,1701.28)]
  Start = (-850.675,618.052,1701.28)
  Subdivisions = 0
FEATURE [Part::Part2DObjectPython] Line062  # Draft 2D object (typed FeaturePython)
  ChamferSize = 0
  Closed = false
  End = (324.937,-1000.03,1701.28)
  FilletRadius = 0
  Length = 1236.11
  MakeFace = true
  MapMode = 5
  Points = (2) [(-850.675,-618.052,1701.28),(324.937,-1000.03,1701.28)]
  Start = (-850.675,-618.052,1701.28)
  Subdivisions = 0
FEATURE [Part::Part2DObjectPython] Line063  # Draft 2D object (typed FeaturePython)
  ChamferSize = 0
  Closed = false
  End = (1051.49,1.332e-09,1701.28)
  FilletRadius = 0
  Length = 1236.1
  MakeFace = true
  MapMode = 5
  Points = (2) [(324.929,1000.03,1701.28),(1051.49,1.3321e-09,1701.28)]
  Start = (324.929,1000.03,1701.28)
  Subdivisions = 0
FEATURE [Part::Part2DObjectPython] Line064  # Draft 2D object (typed FeaturePython)
  ChamferSize = 0
  Closed = false
  End = (324.937,-1000.03,1701.28)
  FilletRadius = 0
  Length = 1236.1
  MakeFace = true
  MapMode = 5
  Points = (2) [(1051.49,1.3321e-09,1701.28),(324.937,-1000.03,1701.28)]
  Start = (1051.49,1.332e-09,1701.28)
  Subdivisions = 0
FEATURE [Part::Feature] Clone001057  label="strutcap077"
  Placement = pos=(-17.7984,-12.9315,1993.75) rot=(0.300929,-0.926151,0.227346;1.92056rad)
  shape: bbox 31.35 x 28.31 x 22.68 mm, 19 faces (baked)
FEATURE [Part::Feature] Cylinder029  label="Cylinder008"
  Placement = pos=(-17.7984,-12.9315,1993.75) rot=(0.376611,0.739148,-0.558413;3.69599rad)
  shape: bbox 821.2 x 600.3 x 295.8 mm, 3 faces (baked)
FEATURE [Part::Feature] Clone001058  label="Hub-019"
  Placement = pos=(-845.374,-614.211,1690.69) rot=(0.320391,0.016792,-0.947137;2.03872rad)
  shape: bbox 52.89 x 52.48 x 37.22 mm, 28 faces (baked)
FEATURE [Part::Feature] Clone001059  label="strutcap078"
  Placement = pos=(-851.64,-595.214,1701.75) rot=(0.399329,0.656651,0.639801;3.91882rad)
  shape: bbox 20.03 x 30.19 x 20.75 mm, 19 faces (baked)
FEATURE [Part::Feature] Clone001060  label="strutcap079"
  Placement = pos=(-866.78,-606.214,1690.18) rot=(0.055489,0.9504,0.306039;3.98098rad)
  shape: bbox 31.55 x 26.91 x 26.68 mm, 19 faces (baked)
FEATURE [Part::Feature] Clone001061  label="strutcap080"
  Placement = pos=(-832.872,-605.127,1707.53) rot=(0.591556,0.192211,0.783018;3.63986rad)
  shape: bbox 30.27 x 27.49 x 25.37 mm, 19 faces (baked)
FEATURE [Part::Feature] Clone001062  label="strutcap081"
  Placement = pos=(-829.243,-626.041,1701.75) rot=(0.652221,-0.288292,0.701067;3.2457rad)
  shape: bbox 31.36 x 25.86 x 20.72 mm, 19 faces (baked)
FEATURE [Part::Feature] Clone001063  label="strutcap082"
  Placement = pos=(-844.383,-637.041,1690.18) rot=(-0.545652,0.692057,-0.472568;3.4603rad)
  shape: bbox 22.9 x 32.27 x 26.72 mm, 19 faces (baked)
FEATURE [Part::Feature] Clone001064  label="strutcap083"
  Placement = pos=(-863.151,-627.127,1684.4) rot=(-0.306822,0.944288,-0.119077;3.84415rad)
  shape: bbox 29.74 x 26.84 x 29.82 mm, 19 faces (baked)
FEATURE [Part::Feature] Cylinder030  label="Varilla-B-modif-011"
  Placement = pos=(-851.641,-593.624,1701.75) rot=(-1e-06,0.707107,0.707107;3.1416rad)
  shape: bbox 10.01 x 1189 x 10 mm, 3 faces (baked)
FEATURE [Part::Feature] Clone001065  label="strutcap084"
  Placement = pos=(6.79873,-20.9232,1993.75) rot=(0.690296,-0.501521,0.521506;2.41724rad)
  shape: bbox 23.54 x 32.47 x 22.68 mm, 19 faces (baked)
FEATURE [App::DocumentObjectGroup] Group011  label="Clave"
  Group = -> [Clone001004,Clone,Clone001065,Clone001057,Clone001049,Clone001015]
FEATURE [Part::Feature] Cylinder031  label="Cylinder009"
  Placement = pos=(6.79873,-20.9232,1993.75) rot=(-0.125384,0.791599,-0.598038;2.95271rad)
  shape: bbox 320.8 x 962 x 295.8 mm, 3 faces (baked)
FEATURE [Part::Feature] Clone001066  label="Hub-020"
  Placement = pos=(322.923,-993.798,1690.69) rot=(0.482777,0.390952,-0.783634;0.910971rad)
  shape: bbox 55.11 x 51.63 x 37.22 mm, 28 faces (baked)
FEATURE [Part::Feature] Clone001067  label="strutcap085"
  Placement = pos=(318.147,-979.1,1707.53) rot=(-0.46391,-0.638529,-0.614059;1.7382rad)
  shape: bbox 23.11 x 31.33 x 25.37 mm, 19 faces (baked)
FEATURE [Part::Feature] Clone001068  label="strutcap086"
  Placement = pos=(302.919,-993.887,1701.75) rot=(0.077008,-0.937624,-0.339015;1.71438rad)
  shape: bbox 31.95 x 22.93 x 20.75 mm, 19 faces (baked)
FEATURE [Part::Feature] Clone001069  label="strutcap087"
  Placement = pos=(308.702,-1011.68,1690.18) rot=(-0.539571,0.841799,-0.015424;4.17481rad)
  shape: bbox 29.86 x 29.01 x 26.68 mm, 19 faces (baked)
FEATURE [Part::Feature] Clone001070  label="strutcap088"
  Placement = pos=(329.714,-1014.7,1684.4) rot=(0.771869,-0.560786,0.299561;2.713rad)
  shape: bbox 22.65 x 31.16 x 29.82 mm, 19 faces (baked)
FEATURE [Part::Feature] Clone001071  label="strutcap089"
  Placement = pos=(344.942,-999.909,1690.18) rot=(0.846307,-0.244693,0.47317;3.42288rad)
  shape: bbox 32.71 x 20 x 26.83 mm, 19 faces (baked)
FEATURE [Part::Feature] Clone001072  label="strutcap090"
  Placement = pos=(339.159,-982.111,1701.75) rot=(0.781158,0.168237,0.601239;4.08322rad)
  shape: bbox 29.92 x 30.42 x 20.72 mm, 19 faces (baked)
FEATURE [Part::Feature] Cylinder032  label="Varilla-B-modif-012"
  Placement = pos=(301.407,-993.395,1701.75) rot=(-0.456971,0.628958,0.628958;3.99886rad)
  shape: bbox 1134 x 376.9 x 10 mm, 3 faces (baked)
FEATURE [Part::Feature] Cylinder033  label="Varilla-B-modif-013"
  Placement = pos=(1037.92,-20.3126,1701.75) rot=(0.908667,-0.295233,-0.295233;1.66643rad)
  shape: bbox 706.8 x 967.7 x 10 mm, 3 faces (baked)
FEATURE [Part::Part2DObjectPython] Line065  # Draft 2D object (typed FeaturePython)
  ChamferSize = 0
  Closed = false
  End = (1376.39,-999.957,1051.5)
  FilletRadius = 0
  Length = 1236.03
  MakeFace = true
  MapMode = 5
  Points = (2) [(324.937,-1000.03,1701.28),(1376.39,-999.957,1051.5)]
  Start = (324.937,-1000.03,1701.28)
  Subdivisions = 0
FEATURE [Part::Feature] Cylinder034  label="Varilla-B-modif-014"
  Placement = pos=(1357.36,-1000.76,1064.14) rot=(0.086928,-0.983946,-0.155865;1.03106rad)
  shape: bbox 1017 x 10.03 x 633.5 mm, 3 faces (baked)
FEATURE [Part::Feature] Clone001073  label="strutcap091"
  Placement = pos=(1357.54,-999.86,1064.43) rot=(0.250583,-0.868506,-0.427675;1.13881rad)
  shape: bbox 30.96 x 20.1 x 29.71 mm, 19 faces (baked)
FEATURE [Part::Feature] Cylinder035  label="Cylinder010"
  Placement = pos=(329.697,1014.7,1684.4) rot=(0.985873,-0.156147,0.060603;3.87249rad)
  shape: bbox 228.1 x 679.5 x 779.7 mm, 3 faces (baked)
FEATURE [Part::Feature] Cylinder036  label="Varilla-B-modif-015"
  Placement = pos=(1357.49,999.919,1064.43) rot=(-0.245397,-0.863791,0.440052;1.14636rad)
  shape: bbox 1017 x 10.05 x 633.5 mm, 3 faces (baked)
FEATURE [Part::Feature] Cylinder037  label="Varilla-B-modif-016"
  Placement = pos=(307.663,1011.8,1689.56) rot=(0.557122,0.830163,0.021082;4.15722rad)
  shape: bbox 824.6 x 603.3 x 634.3 mm, 3 faces (baked)
FEATURE [Part::Feature] Clone001074  label="strutcap092"
  Placement = pos=(344.925,999.915,1690.18) rot=(0.847741,0.241212,0.472389;2.87537rad)
  shape: bbox 32.7 x 20 x 26.9 mm, 19 faces (baked)
FEATURE [Part::Feature] Clone001075  label="strutcap093"
  Placement = pos=(329.697,1014.7,1684.4) rot=(0.771865,0.560793,0.299559;3.57019rad)
  shape: bbox 22.65 x 31.16 x 29.82 mm, 19 faces (baked)
FEATURE [Part::Feature] Clone001076  label="strutcap094"
  Placement = pos=(308.478,1011.53,1690.32) rot=(0.543251,0.839537,0.007414;4.18045rad)
  shape: bbox 29.9 x 28.94 x 26.61 mm, 19 faces (baked)
FEATURE [Part::Feature] Clone001077  label="strutcap095"
  Placement = pos=(1357.49,999.919,1064.43) rot=(-0.246268,-0.855952,0.454641;1.14624rad)
  shape: bbox 30.92 x 20 x 29.82 mm, 19 faces (baked)
FEATURE [Part::Feature] Cylinder038  label="Varilla-B-modif-017"
  Placement = pos=(-867.207,605.268,1689.56) rot=(-0.035573,0.954465,-0.296196;3.97386rad)
  shape: bbox 825.4 x 602.3 x 634.3 mm, 3 faces (baked)
FEATURE [Part::Feature] Cylinder039  label="Cylinder011"
  Placement = pos=(-863.157,627.12,1684.4) rot=(0.877489,0.447103,-0.173528;3.79809rad)
  shape: bbox 579.9 x 424.4 x 779.7 mm, 3 faces (baked)
FEATURE [Part::Feature] Cylinder040  label="Varilla-B-modif-018"
  Placement = pos=(-531.491,1600.04,1064.43) rot=(0.199138,-0.542979,0.815793;2.00203rad)
  shape: bbox 322.2 x 967.7 x 633.5 mm, 3 faces (baked)
FEATURE [Part::Feature] Cylinder041  label="Varilla-B-modif-019"
  Placement = pos=(-1685.97,-11.0365,1064.43) rot=(0.404604,-0.271467,0.87327;3.07625rad)
  shape: bbox 825.4 x 603.1 x 633.5 mm, 3 faces (baked)
FEATURE [Part::Feature] Cylinder042  label="Cylinder012"
  Placement = pos=(-863.157,-627.12,1684.4) rot=(0.42906,0.842077,-0.326825;3.47161rad)
  shape: bbox 579.9 x 424.4 x 779.7 mm, 3 faces (baked)
FEATURE [Part::Feature] Cylinder043  label="Varilla-B-modif-020"
  Placement = pos=(-843.626,-637.725,1689.56) rot=(-0.547223,0.697036,-0.463345;3.47876rad)
  shape: bbox 321.4 x 967.4 x 634.3 mm, 3 faces (baked)
FEATURE [Part::Feature] Cylinder044  label="Varilla-B-modif-021"
  Placement = pos=(-510.484,-1606.87,1064.43) rot=(0.55703,0.020822,0.830232;4.15797rad)
  shape: bbox 825.4 x 603 x 633.5 mm, 3 faces (baked)
FEATURE [Part::Feature] Cylinder045  label="Cylinder013"
  Placement = pos=(329.705,-1014.7,1684.4) rot=(-0.146074,0.922248,-0.35794;3.02833rad)
  shape: bbox 228.1 x 679.5 x 779.7 mm, 3 faces (baked)
FEATURE [Part::Feature] Cylinder046  label="Cylinder014"
  Placement = pos=(540.281,1707.78,876.414) rot=(0.752998,0.648404,-0.1121;3.71301rad)
  shape: bbox 538.6 x 295.9 x 862.3 mm, 3 faces (baked)
FEATURE [Part::Feature] Cylinder047  label="Cylinder015"
  Placement = pos=(565.816,1699.57,875.771) rot=(0.764557,0.607953,0.214116;2.70375rad)
  shape: bbox 604.8 x 89.65 x 862.6 mm, 3 faces (baked)
FEATURE [Part::Feature] Cylinder048  label="Varilla-B-modif-022"
  Placement = pos=(22.9176,1992.61,-2.89e-13) rot=(0.697446,0.506739,0.506739;1.92357rad)
  shape: bbox 1134 x 376.8 x 10 mm, 3 faces (baked)
FEATURE [Part::Feature] Cylinder049  label="Cylinder016"
  Placement = pos=(-1457.24,1041.57,876.414) rot=(0.221853,0.940826,-0.256178;3.47269rad)
  shape: bbox 445.1 x 424.7 x 862.3 mm, 3 faces (baked)
FEATURE [Part::Feature] Cylinder050  label="Varilla-B-modif-023"
  Placement = pos=(-1888,637.545,-2.89e-13) rot=(0.223909,0.689153,0.689153;2.70104rad)
  shape: bbox 706.8 x 967.7 x 10 mm, 3 faces (baked)
FEATURE [Part::Feature] Cylinder051  label="Cylinder017"
  Placement = pos=(-1441.54,1063.32,875.771) rot=(0.255317,0.92006,0.297158;3.03584rad)
  shape: bbox 269.8 x 551.3 x 862.6 mm, 3 faces (baked)
FEATURE [Part::Feature] Cylinder052  label="Varilla-B-modif-024"
  Placement = pos=(-1189.77,-1598.58,-2.89e-13) rot=(-0.223929,0.68915,0.68915;3.58218rad)
  shape: bbox 706.9 x 967.6 x 10 mm, 3 faces (baked)
FEATURE [Part::Feature] Cylinder053  label="Cylinder018"
  Placement = pos=(-1440.9,-1064.05,876.414) rot=(-0.368456,0.879459,-0.301316;3.11119rad)
  shape: bbox 270.1 x 551.7 x 862.3 mm, 3 faces (baked)
FEATURE [Part::Feature] Cylinder054  label="Cylinder019"
  Placement = pos=(-1456.73,-1042.4,875.771) rot=(-0.336706,0.901009,0.273516;3.40569rad)
  shape: bbox 444.9 x 424.3 x 862.6 mm, 3 faces (baked)
FEATURE [Part::Feature] Cylinder055  label="Cylinder020"
  Placement = pos=(541.239,-1707.55,875.771) rot=(0.824708,-0.546051,-0.147262;2.60334rad)
  shape: bbox 538.1 x 295.8 x 862.6 mm, 3 faces (baked)
FEATURE [Part::Feature] Cylinder056  label="Varilla-B-modif-025"
  Placement = pos=(1152.7,-1625.51,0) rot=(0.69747,-0.506723,-0.506723;1.92354rad)
  shape: bbox 1134 x 376.9 x 10 mm, 3 faces (baked)
FEATURE [Part::Feature] Cylinder057  label="Cylinder021"
  Placement = pos=(566.724,-1699.19,876.414) rot=(0.829948,-0.503984,0.239135;3.52267rad)
  shape: bbox 605.2 x 89.84 x 862.3 mm, 3 faces (baked)
FEATURE [Part::Feature] Clone001078  label="strutcap096"
  Placement = pos=(530.378,1699.18,898.82) rot=(-0.414259,-0.732085,0.540778;1.78299rad)
  shape: bbox 30.96 x 20.14 x 22.38 mm, 19 faces (baked)
FEATURE [Part::Feature] Clone001079  label="strutcap097"
  Placement = pos=(540.273,1707.74,876.408) rot=(0.753174,0.648286,-0.111595;3.71391rad)
  shape: bbox 26.59 x 25.55 x 30.67 mm, 19 faces (baked)
FEATURE [Part::Feature] Clone001080  label="strutcap098"
  Placement = pos=(565.808,1699.53,875.769) rot=(0.764338,0.608049,0.214624;2.70459rad)
  shape: bbox 28.6 x 20 x 30.68 mm, 19 faces (baked)
FEATURE [Part::Feature] Clone001081  label="strutcap099"
  Placement = pos=(570.601,1687.09,896.949) rot=(0.782815,0.102142,0.613814;1.95118rad)
  shape: bbox 32 x 28.57 x 22.88 mm, 19 faces (baked)
FEATURE [Part::Feature] Clone001082  label="strutcap100"
  Placement = pos=(548.01,1686.6,911.365) rot=(0.323892,-0.445799,0.83448;1.43273rad)
  shape: bbox 21.5 x 28.59 x 31.71 mm, 19 faces (baked)
FEATURE [Part::Feature] Clone001083  label="Hub5-01-clave004"
  Placement = pos=(549.337,1690.68,888.915) rot=(0.403006,0.403003,0.82169;3.9346rad)
  shape: bbox 54.11 x 37.29 x 51.33 mm, 25 faces (baked)
FEATURE [Part::Feature] Clone001084  label="Hub5-01-clave005"
  Placement = pos=(-1438.18,1044.9,888.915) rot=(-0.126077,-0.795998,-0.592023;1.42128rad)
  shape: bbox 45.2 x 49.91 x 51.33 mm, 25 faces (baked)
FEATURE [Part::Feature] Clone001085  label="strutcap101"
  Placement = pos=(-1457.21,1041.55,876.408) rot=(0.222054,0.940813,-0.256052;3.47399rad)
  shape: bbox 28.2 x 24.81 x 30.67 mm, 19 faces (baked)
FEATURE [Part::Feature] Clone001086  label="strutcap102"
  Placement = pos=(-1441.51,1063.3,875.769) rot=(0.255103,0.920065,0.297325;3.03711rad)
  shape: bbox 22.21 x 29.03 x 30.68 mm, 19 faces (baked)
FEATURE [Part::Feature] Clone001087  label="strutcap103"
  Placement = pos=(-1428.19,1064.01,896.949) rot=(0.480485,0.454913,0.749792;2.83064rad)
  shape: bbox 30.89 x 29.5 x 22.88 mm, 19 faces (baked)
FEATURE [Part::Feature] Clone001088  label="strutcap104"
  Placement = pos=(-1434.71,1042.38,911.365) rot=(0.359362,-0.116764,0.925865;2.55715rad)
  shape: bbox 27.2 x 24.82 x 31.71 mm, 19 faces (baked)
FEATURE [Part::Feature] Clone001089  label="strutcap105"
  Placement = pos=(-1452.12,1029.49,898.82) rot=(0.076698,-0.673574,0.735129;2.61355rad)
  shape: bbox 25.23 x 31.29 x 22.38 mm, 19 faces (baked)
FEATURE [Part::Feature] Clone001090  label="Hub5-01-clave006"
  Placement = pos=(-1438.18,-1044.9,888.915) rot=(0.440106,-0.863765,0.245392;1.14634rad)
  shape: bbox 45.2 x 49.91 x 51.33 mm, 25 faces (baked)
FEATURE [Part::Feature] Clone001091  label="strutcap106"
  Placement = pos=(-1456.71,-1042.38,875.769) rot=(-0.336923,0.900992,0.273307;3.40693rad)
  shape: bbox 28.13 x 24.8 x 30.68 mm, 19 faces (baked)
FEATURE [Part::Feature] Clone001092  label="strutcap107"
  Placement = pos=(-1453.27,-1029.49,896.949) rot=(0.126083,0.675935,0.726096;3.77224rad)
  shape: bbox 25.11 x 31.29 x 22.88 mm, 19 faces (baked)
FEATURE [Part::Feature] Clone001093  label="strutcap108"
  Placement = pos=(-1434.71,-1042.38,911.365) rot=(0.359362,0.116764,0.925865;3.72603rad)
  shape: bbox 27.2 x 24.82 x 31.71 mm, 19 faces (baked)
FEATURE [Part::Feature] Clone001094  label="strutcap109"
  Placement = pos=(-1427.84,-1062.91,898.82) rot=(0.451787,-0.493106,0.743461;3.55656rad)
  shape: bbox 30.89 x 29.64 x 22.38 mm, 19 faces (baked)
FEATURE [Part::Feature] Clone001095  label="strutcap110"
  Placement = pos=(-1440.88,-1064.03,876.408) rot=(-0.368245,0.879462,-0.301567;3.11241rad)
  shape: bbox 22.22 x 29.51 x 30.67 mm, 19 faces (baked)
FEATURE [Part::Feature] Clone001096  label="Hub5-01-clave007"
  Placement = pos=(549.351,-1690.68,888.915) rot=(0.58635,-0.29876,0.752952;1.85083rad)
  shape: bbox 54.11 x 37.29 x 51.33 mm, 25 faces (baked)
FEATURE [Part::Feature] Clone001097  label="strutcap111"
  Placement = pos=(530.035,-1700.27,896.949) rot=(0.372241,-0.78273,-0.49877;1.70887rad)
  shape: bbox 30.96 x 20.06 x 22.88 mm, 19 faces (baked)
FEATURE [Part::Feature] Clone001098  label="strutcap112"
  Placement = pos=(541.226,-1707.52,875.769) rot=(0.824895,-0.545917,-0.146708;2.60259rad)
  shape: bbox 26.57 x 25.89 x 30.68 mm, 19 faces (baked)
FEATURE [Part::Feature] Clone001099  label="strutcap113"
  Placement = pos=(548.024,-1686.6,911.365) rot=(-0.323892,-0.445802,-0.834479;1.43272rad)
  shape: bbox 21.5 x 28.59 x 31.71 mm, 19 faces (baked)
FEATURE [Part::Feature] Clone001100  label="strutcap114"
  Placement = pos=(569.68,-1686.41,898.82) rot=(-0.797368,0.162279,-0.581265;1.86885rad)
  shape: bbox 32.15 x 28.57 x 22.38 mm, 19 faces (baked)
FEATURE [Part::Feature] Clone001101  label="strutcap115"
  Placement = pos=(566.711,-1699.15,876.408) rot=(0.829728,-0.504084,0.239691;3.52197rad)
  shape: bbox 29.43 x 20.13 x 30.67 mm, 19 faces (baked)
FEATURE [Part::Feature] Clone001102  label="Hub-021"
  Placement = pos=(-522.419,1607.96,1044.94) rot=(-0.404151,-0.556253,-0.726117;1.57141rad)
  shape: bbox 54.14 x 40.13 x 50.11 mm, 28 faces (baked)
FEATURE [Part::Feature] Clone001105  label="strutcap118"
  Placement = pos=(-516.067,1625.93,1032.31) rot=(0.655766,0.705688,0.268283;3.03581rad)
  shape: bbox 25.3 x 25.97 x 30.96 mm, 19 faces (baked)
FEATURE [Part::Feature] Clone001106  label="strutcap119"
  Placement = pos=(-503.124,1619.77,1048.2) rot=(0.67398,0.417938,0.609162;2.53046rad)
  shape: bbox 30.99 x 22.33 x 20.3 mm, 19 faces (baked)
FEATURE [Part::Feature] Clone001107  label="strutcap120"
  Placement = pos=(-510.484,1606.82,1064.4) rot=(0.551632,-0.035834,0.833318;2.11859rad)
  shape: bbox 28.95 x 26.75 x 29.86 mm, 19 faces (baked)
FEATURE [Part::Feature] Clone001108  label="strutcap121"
  Placement = pos=(-531.49,1600.04,1064.43) rot=(0.195018,-0.537301,0.820534;2.01296rad)
  shape: bbox 24.18 x 30.56 x 29.82 mm, 19 faces (baked)
FEATURE [Part::Feature] Clone001109  label="Hub-022"
  Placement = pos=(-1690.7,0.0372864,1044.94) rot=(-1.1e-05,-1,-2e-05;1.01578rad)
  shape: bbox 37.43 x 53.16 x 50.11 mm, 28 faces (baked)
FEATURE [Part::Feature] Clone001111  label="strutcap123"
  Placement = pos=(-1705.82,11.6304,1032.31) rot=(0.116339,0.961371,0.249462;3.3715rad)
  shape: bbox 23.88 x 27.32 x 30.96 mm, 19 faces (baked)
FEATURE [Part::Feature] Clone001112  label="strutcap124"
  Placement = pos=(-1695.97,22.0374,1048.2) rot=(0.287109,0.703654,0.649954;3.33809rad)
  shape: bbox 21.94 x 32.05 x 20.3 mm, 19 faces (baked)
FEATURE [Part::Feature] Clone001113  label="strutcap125"
  Placement = pos=(-1685.93,11.0372,1064.4) rot=(0.407724,0.257586,0.87602;3.20384rad)
  shape: bbox 29.33 x 26.91 x 29.86 mm, 19 faces (baked)
FEATURE [Part::Feature] Clone001114  label="strutcap126"
  Placement = pos=(-1685.97,-11.0364,1064.43) rot=(0.40029,-0.270519,0.87555;3.09124rad)
  shape: bbox 29.19 x 27.26 x 29.82 mm, 19 faces (baked)
FEATURE [Part::Feature] Clone001116  label="Hub-023"
  Placement = pos=(-522.49,-1607.94,1044.94) rot=(0.404145,-0.55627,0.726106;1.57137rad)
  shape: bbox 54.14 x 40.13 x 50.11 mm, 28 faces (baked)
FEATURE [Part::Feature] Clone001117  label="strutcap128"
  Placement = pos=(-510.498,-1606.87,1064.43) rot=(0.555204,0.018892,0.8315;4.17521rad)
  shape: bbox 29.12 x 26.51 x 29.82 mm, 19 faces (baked)
FEATURE [Part::Feature] Clone001118  label="strutcap129"
  Placement = pos=(-531.478,-1600,1064.4) rot=(-0.211892,-0.532008,-0.819798;2.00111rad)
  shape: bbox 23.74 x 30.6 x 29.86 mm, 19 faces (baked)
FEATURE [Part::Feature] Clone001119  label="strutcap130"
  Placement = pos=(-545.042,-1606.15,1048.2) rot=(-0.203171,0.82696,0.52427;4.09656rad)
  shape: bbox 32.67 x 26.78 x 20.3 mm, 19 faces (baked)
FEATURE [Part::Feature] Clone001120  label="strutcap131"
  Placement = pos=(-538.189,-1618.74,1032.31) rot=(-0.481748,0.865531,0.13702;3.62315rad)
  shape: bbox 28.95 x 20.82 x 30.96 mm, 19 faces (baked)
FEATURE [Part::Feature] Cylinder058  label="Cylinder022"
  Placement = pos=(530.378,1699.21,898.834) rot=(-0.413717,-0.732343,0.540844;1.78399rad)
  shape: bbox 1035 x 89.07 x 159.4 mm, 3 faces (baked)
FEATURE [Part::Feature] Cylinder059  label="Cylinder023"
  Placement = pos=(570.617,1687.11,896.969) rot=(0.783276,0.101681,0.613303;1.95105rad)
  shape: bbox 795.2 x 679.7 x 161.3 mm, 3 faces (baked)
FEATURE [Part::Feature] Cylinder060  label="Varilla-B-modif-026"
  Placement = pos=(1372.43,1012.12,1030.9) rot=(0.616123,0.772286,0.154811;3.60091rad)
  shape: bbox 201.9 x 602.9 x 1017 mm, 3 faces (baked)
FEATURE [Part::Feature] Clone001123  label="strutcap134"
  Placement = pos=(1359.16,1014.63,1048.2) rot=(-0.756432,-0.638991,0.139644;1.73831rad)
  shape: bbox 30 x 31.16 x 20.3 mm, 19 faces (baked)
FEATURE [Part::Feature] Clone001124  label="strutcap135"
  Placement = pos=(1373.75,1011.64,1032.01) rot=(0.909322,0.414351,0.038035;3.6661rad)
  shape: bbox 20.28 x 29.06 x 31.05 mm, 19 faces (baked)
FEATURE [Part::Feature] Clone001125  label="Hub-024"
  Placement = pos=(1167.88,1607.21,-5e-15) rot=(-0.413351,0.811346,0.413351;1.77835rad)
  shape: bbox 48.34 x 39.86 x 55.6 mm, 28 faces (baked)
FEATURE [Part::Feature] Clone001126  label="strutcap136"
  Placement = pos=(1162.63,1618.69,19.0526) rot=(-0.354648,-0.474559,0.805617;1.14619rad)
  shape: bbox 28.01 x 22.72 x 31.69 mm, 19 faces (baked)
FEATURE [Part::Feature] Clone001127  label="strutcap137"
  Placement = pos=(1153.73,1625.15,0) rot=(-0.697483,-0.506713,0.506713;1.92352rad)
  shape: bbox 31.34 x 25.98 x 20 mm, 19 faces (baked)
FEATURE [Part::Feature] Clone001128  label="strutcap138"
  Placement = pos=(1180.54,1607.1,19.8831) rot=(0.632762,0.03188,0.77369;0.99253rad)
  shape: bbox 25.27 x 26.79 x 31.62 mm, 19 faces (baked)
FEATURE [Part::Feature] Clone001129  label="strutcap139"
  Placement = pos=(1189.16,1599.52,-2.5e-14) rot=(0.908302,0.295794,0.295794;1.66683rad)
  shape: bbox 30.1 x 30.58 x 20 mm, 19 faces (baked)
FEATURE [Part::Feature] Cylinder061  label="Varilla-B-modif-027"
  Placement = pos=(1189.84,1598.52,-2.89e-13) rot=(0.908667,0.295233,0.295233;1.66643rad)
  shape: bbox 706.8 x 967.7 x 10 mm, 3 faces (baked)
FEATURE [Part::Feature] Cylinder062  label="Varilla-B-modif-028"
  Placement = pos=(-538.473,1618.02,1030.9) rot=(0.045055,0.998909,-0.012317;3.69415rad)
  shape: bbox 633 x 11.04 x 1017 mm, 3 faces (baked)
FEATURE [Part::Feature] Cylinder063  label="Varilla-B-modif-029"
  Placement = pos=(-10.1769,1992.61,20.4541) rot=(0.167218,-0.60597,0.777714;0.899398rad)
  shape: bbox 514.7 x 376.9 x 1017 mm, 3 faces (baked)
FEATURE [Part::Feature] Cylinder064  label="Cylinder024"
  Placement = pos=(-1428.21,1064.04,896.969) rot=(0.481026,0.454827,0.749497;2.83001rad)
  shape: bbox 888.2 x 550.9 x 161.3 mm, 3 faces (baked)
FEATURE [Part::Feature] Clone001130  label="strutcap140"
  Placement = pos=(-544.971,1606.18,1048.2) rot=(0.203272,0.826904,-0.52432;4.09647rad)
  shape: bbox 32.67 x 26.78 x 20.3 mm, 19 faces (baked)
FEATURE [Part::Feature] Clone001131  label="strutcap141"
  Placement = pos=(-537.612,1619.12,1032.01) rot=(0.488533,0.863387,-0.126091;3.6085rad)
  shape: bbox 28.61 x 21.1 x 31.05 mm, 19 faces (baked)
FEATURE [Part::Feature] Cylinder065  label="Cylinder025"
  Placement = pos=(-1453.3,-1029.5,896.969) rot=(0.126564,0.676057,0.725898;3.77131rad)
  shape: bbox 252.7 x 1010 x 161.3 mm, 3 faces (baked)
FEATURE [Part::Feature] Cylinder066  label="Cylinder026"
  Placement = pos=(-1452.15,1029.5,898.834) rot=(0.077196,-0.673675,0.734984;2.61448rad)
  shape: bbox 253.8 x 1010 x 159.4 mm, 3 faces (baked)
FEATURE [Part::Feature] Cylinder067  label="Varilla-B-modif-030"
  Placement = pos=(-1898.23,606.07,20.4541) rot=(0.251906,-0.2009,0.946669;2.02469rad)
  shape: bbox 203 x 603 x 1017 mm, 3 faces (baked)
FEATURE [Part::Feature] Cylinder068  label="Varilla-B-modif-031"
  Placement = pos=(-1705.23,-12.1218,1030.9) rot=(-0.54234,0.821957,-0.173938;3.57234rad)
  shape: bbox 203.8 x 602.3 x 1017 mm, 3 faces (baked)
FEATURE [Part::Feature] Clone001132  label="strutcap142"
  Placement = pos=(-1695.97,-21.9626,1048.2) rot=(-0.287012,0.703678,-0.64997;3.33796rad)
  shape: bbox 21.94 x 32.05 x 20.3 mm, 19 faces (baked)
FEATURE [Part::Feature] Clone001133  label="strutcap143"
  Placement = pos=(-1706.01,-10.9624,1032.01) rot=(-0.109939,0.96532,-0.236791;3.37221rad)
  shape: bbox 24.01 x 26.91 x 31.05 mm, 19 faces (baked)
FEATURE [Part::Feature] Cylinder069  label="Cylinder027"
  Placement = pos=(-1427.84,-1062.95,898.834) rot=(0.452335,-0.492994,0.743203;3.55725rad)
  shape: bbox 887.9 x 551.9 x 159.4 mm, 3 faces (baked)
FEATURE [Part::Feature] Cylinder070  label="Cylinder028"
  Placement = pos=(530.036,-1700.3,896.969) rot=(0.371723,-0.782962,-0.498791;1.70995rad)
  shape: bbox 1035 x 90.15 x 161.3 mm, 3 faces (baked)
FEATURE [Part::Feature] Cylinder071  label="Varilla-B-modif-032"
  Placement = pos=(-515.403,-1625.52,1030.9) rot=(0.903009,-0.3391,0.263791;2.99542rad)
  shape: bbox 513.7 x 377.4 x 1017 mm, 3 faces (baked)
FEATURE [Part::Feature] Cylinder072  label="Varilla-B-modif-033"
  Placement = pos=(-1162.98,-1618.04,20.4541) rot=(0.273237,-0.012278,0.961868;3.22808rad)
  shape: bbox 633.5 x 10.03 x 1017 mm, 3 faces (baked)
FEATURE [Part::Feature] Clone001134  label="strutcap144"
  Placement = pos=(-503.182,-1619.75,1048.2) rot=(0.673934,-0.418028,0.609152;3.75287rad)
  shape: bbox 30.99 x 22.33 x 20.3 mm, 19 faces (baked)
FEATURE [Part::Feature] Clone001135  label="strutcap145"
  Placement = pos=(-516.746,-1625.9,1032.01) rot=(-0.652655,0.712308,-0.258186;3.0512rad)
  shape: bbox 24.88 x 26 x 31.05 mm, 19 faces (baked)
FEATURE [Part::Feature] Cylinder073  label="Cylinder029"
  Placement = pos=(569.712,-1686.43,898.834) rot=(-0.797837,0.161779,-0.580762;1.86862rad)
  shape: bbox 796.1 x 679.1 x 159.4 mm, 3 faces (baked)
FEATURE [Part::Feature] Cylinder074  label="Varilla-B-modif-034"
  Placement = pos=(1179.48,-1606.05,20.4541) rot=(-0.285022,-0.188133,-0.939877;1.85504rad)
  shape: bbox 203 x 603.1 x 1017 mm, 3 faces (baked)
FEATURE [Part::Feature] Clone001136  label="Hub-025"
  Placement = pos=(0.0486416,1986.72,-5e-15) rot=(-0.577341,0.577369,0.577341;2.09437rad)
  shape: bbox 53.16 x 12.4 x 55.6 mm, 28 faces (baked)
FEATURE [Part::Feature] Clone001137  label="strutcap146"
  Placement = pos=(-21.9511,1992.92,0) rot=(0.456975,0.628957,-0.628957;3.99887rad)
  shape: bbox 32.2 x 23.31 x 20 mm, 19 faces (baked)
FEATURE [Part::Feature] Clone001138  label="strutcap147"
  Placement = pos=(-10.9511,1992.92,19.0526) rot=(-0.043067,-0.321506,0.945927;1.61128rad)
  shape: bbox 24.46 x 22.68 x 32.46 mm, 19 faces (baked)
FEATURE [Part::Feature] Clone001139  label="strutcap148"
  Placement = pos=(10.3528,1994.07,19.8831) rot=(0.407648,0.155548,0.899793;1.52684rad)
  shape: bbox 27.6 x 22.68 x 31.62 mm, 19 faces (baked)
FEATURE [Part::Feature] Clone001140  label="strutcap149"
  Placement = pos=(21.7815,1993.01,-2.5e-14) rot=(0.696937,0.507089,0.507089;1.92426rad)
  shape: bbox 32.2 x 23.29 x 20 mm, 19 faces (baked)
FEATURE [Part::Feature] Cylinder075  label="Varilla-B-modif-035"
  Placement = pos=(-1152.6,1625.58,-2.89e-13) rot=(0.456975,0.628957,0.628957;2.28431rad)
  shape: bbox 1134 x 376.9 x 10 mm, 3 faces (baked)
FEATURE [Part::Feature] Clone001141  label="Hub-026"
  Placement = pos=(-1889.47,613.977,-5e-15) rot=(0.702712,-0.111316,-0.702712;3.36331rad)
  shape: bbox 27.47 x 52.09 x 55.6 mm, 28 faces (baked)
FEATURE [Part::Feature] Clone001142  label="strutcap150"
  Placement = pos=(-1898.77,605.432,19.0526) rot=(0.112612,-0.208529,0.971511;2.82156rad)
  shape: bbox 20.37 x 25.38 x 32.46 mm, 19 faces (baked)
FEATURE [Part::Feature] Clone001143  label="strutcap151"
  Placement = pos=(-1902.17,594.971,0) rot=(8e-06,0.707107,-0.707107;3.14161rad)
  shape: bbox 20.3 x 30 x 20 mm, 19 faces (baked)
FEATURE [Part::Feature] Clone001144  label="strutcap152"
  Placement = pos=(-1893.28,626.049,19.8831) rot=(0.168898,0.258947,0.95101;2.70038rad)
  shape: bbox 25.15 x 27.06 x 31.62 mm, 19 faces (baked)
FEATURE [Part::Feature] Clone001145  label="strutcap153"
  Placement = pos=(-1888.73,636.589,-2.5e-14) rot=(0.22342,0.689233,0.689233;2.70197rad)
  shape: bbox 27.81 x 32.24 x 20 mm, 19 faces (baked)
FEATURE [Part::Feature] Clone001146  label="Hub-027"
  Placement = pos=(-1167.76,1607.29,-5e-15) rot=(0.665244,-0.33897,-0.665244;3.79522rad)
  shape: bbox 48.34 x 39.85 x 55.6 mm, 28 faces (baked)
FEATURE [Part::Feature] Clone001147  label="strutcap154"
  Placement = pos=(-1180.31,1605.85,19.0526) rot=(0.047109,-0.257408,0.965154;2.21275rad)
  shape: bbox 22.76 x 25.45 x 32.46 mm, 19 faces (baked)
FEATURE [Part::Feature] Clone001148  label="strutcap155"
  Placement = pos=(-1189.21,1599.38,0) rot=(0.223919,0.689152,-0.689152;3.58216rad)
  shape: bbox 30.09 x 30.59 x 20 mm, 19 faces (baked)
FEATURE [Part::Feature] Clone001149  label="strutcap156"
  Placement = pos=(-1163.75,1619.3,19.8831) rot=(0.270223,0.217936,0.937808;2.10624rad)
  shape: bbox 27.56 x 22.35 x 31.62 mm, 19 faces (baked)
FEATURE [Part::Feature] Clone001150  label="strutcap157"
  Placement = pos=(-1153.87,1625.15,-2.5e-14) rot=(0.456433,0.629154,0.629154;2.28521rad)
  shape: bbox 31.34 x 26 x 20 mm, 19 faces (baked)
FEATURE [Part::Feature] Cylinder076  label="Varilla-B-modif-036"
  Placement = pos=(-1902.18,-593.911,-2.89e-13) rot=(-2e-06,0.707107,0.707107;3.1416rad)
  shape: bbox 10.01 x 1189 x 10 mm, 3 faces (baked)
FEATURE [Part::Feature] Clone001151  label="Hub-028"
  Placement = pos=(-1889.51,-613.843,-5e-15) rot=(0.702716,0.111274,-0.702716;2.91996rad)
  shape: bbox 27.47 x 52.09 x 55.6 mm, 28 faces (baked)
FEATURE [Part::Feature] Clone001152  label="strutcap158"
  Placement = pos=(-1888.61,-636.682,0) rot=(-0.223903,0.689154,-0.689154;2.70105rad)
  shape: bbox 27.82 x 32.23 x 20 mm, 19 faces (baked)
FEATURE [Part::Feature] Clone001153  label="strutcap159"
  Placement = pos=(-1892.01,-626.22,19.0526) rot=(0.171151,-0.163157,0.971641;3.43228rad)
  shape: bbox 24.41 x 24.08 x 32.46 mm, 19 faces (baked)
FEATURE [Part::Feature] Clone001154  label="strutcap160"
  Placement = pos=(-1899.69,-606.315,19.8831) rot=(0.078906,0.292136,0.953116;3.29902rad)
  shape: bbox 20 x 27.5 x 31.62 mm, 19 faces (baked)
FEATURE [Part::Feature] Clone001155  label="strutcap161"
  Placement = pos=(-1902.21,-595.116,-2.5e-14) rot=(-0.00048,0.707107,0.707107;3.14255rad)
  shape: bbox 20.33 x 30.01 x 20 mm, 19 faces (baked)
FEATURE [Part::Feature] Clone001156  label="Hub-029"
  Placement = pos=(-1167.81,-1607.26,-5e-15) rot=(-0.665251,-0.338942,0.665251;3.79517rad)
  shape: bbox 48.34 x 39.86 x 55.6 mm, 28 faces (baked)
FEATURE [Part::Feature] Clone001157  label="strutcap162"
  Placement = pos=(-1180.46,-1607.15,19.8831) rot=(-0.016336,0.32408,0.945889;3.89619rad)
  shape: bbox 25.27 x 26.79 x 31.62 mm, 19 faces (baked)
FEATURE [Part::Feature] Clone001158  label="strutcap163"
  Placement = pos=(-1189.08,-1599.57,-2.5e-14) rot=(-0.224418,0.689071,0.689071;3.58311rad)
  shape: bbox 30.1 x 30.58 x 20 mm, 19 faces (baked)
FEATURE [Part::Feature] Clone001159  label="strutcap164"
  Placement = pos=(-1162.55,-1618.75,19.0526) rot=(0.234252,-0.112384,0.965658;4.04131rad)
  shape: bbox 25.78 x 20.67 x 32.46 mm, 19 faces (baked)
FEATURE [Part::Feature] Clone001160  label="strutcap165"
  Placement = pos=(-1153.65,-1625.21,0) rot=(-0.456958,0.628963,-0.628963;2.28434rad)
  shape: bbox 31.34 x 25.98 x 20 mm, 19 faces (baked)
FEATURE [Part::Feature] Cylinder077  label="Varilla-B-modif-037"
  Placement = pos=(-22.8736,-1992.61,-2.89e-13) rot=(-0.456985,0.628953,0.628953;3.99889rad)
  shape: bbox 1134 x 376.8 x 10 mm, 3 faces (baked)
FEATURE [Part::Feature] Clone001161  label="Hub-030"
  Placement = pos=(0.0119054,-1986.72,-5e-15) rot=(-0.577354,-0.577343,0.577354;4.18878rad)
  shape: bbox 53.16 x 12.4 x 55.6 mm, 28 faces (baked)
FEATURE [Part::Feature] Clone001162  label="strutcap166"
  Placement = pos=(-10.292,-1994.07,19.8831) rot=(0.137371,-0.359993,-0.922786;1.79868rad)
  shape: bbox 27.6 x 22.68 x 31.62 mm, 19 faces (baked)
FEATURE [Part::Feature] Clone001163  label="strutcap167"
  Placement = pos=(11.0118,-1992.92,19.0526) rot=(-0.317192,0.042484,-0.947409;1.63983rad)
  shape: bbox 24.46 x 22.68 x 32.46 mm, 19 faces (baked)
FEATURE [Part::Feature] Clone001164  label="strutcap168"
  Placement = pos=(22.0118,-1992.92,0) rot=(-0.69746,0.50673,-0.50673;1.92355rad)
  shape: bbox 32.2 x 23.31 x 20 mm, 19 faces (baked)
FEATURE [Part::Feature] Clone001165  label="strutcap169"
  Placement = pos=(-21.7208,-1993.01,-2.5e-14) rot=(-0.457503,0.628765,0.628765;3.99974rad)
  shape: bbox 32.2 x 23.29 x 20 mm, 19 faces (baked)
FEATURE [Part::Feature] Clone001166  label="Hub-031"
  Placement = pos=(1167.8,-1607.27,-5e-15) rot=(0.413386,0.81131,-0.413386;1.77839rad)
  shape: bbox 48.34 x 39.86 x 55.6 mm, 28 faces (baked)
FEATURE [Part::Feature] Clone001167  label="strutcap170"
  Placement = pos=(1163.78,-1619.27,19.8831) rot=(0.326774,-0.405165,-0.85385;1.23636rad)
  shape: bbox 27.56 x 22.35 x 31.62 mm, 19 faces (baked)
FEATURE [Part::Feature] Clone001168  label="strutcap171"
  Placement = pos=(1180.34,-1605.82,19.0526) rot=(-0.455439,-0.083356,-0.886356;1.05951rad)
  shape: bbox 22.76 x 25.45 x 32.46 mm, 19 faces (baked)
FEATURE [Part::Feature] Clone001169  label="strutcap172"
  Placement = pos=(1153.91,-1625.13,-2.5e-14) rot=(0.697993,-0.506363,-0.506363;1.92284rad)
  shape: bbox 31.34 x 26 x 20 mm, 19 faces (baked)
FEATURE [Part::Feature] Clone001170  label="strutcap173"
  Placement = pos=(1189.24,-1599.35,0) rot=(-0.908667,0.295233,-0.295233;1.66643rad)
  shape: bbox 30.09 x 30.59 x 20 mm, 19 faces (baked)
FEATURE [Part::Feature] Cylinder078  label="Varilla-B-modif-038"
  Placement = pos=(1888.01,-637.504,0) rot=(0.908674,-0.295221,-0.295221;1.66642rad)
  shape: bbox 706.8 x 967.7 x 10 mm, 3 faces (baked)
FEATURE [App::DocumentObjectGroup] Group010  label="Estructura"
  Group = -> [Clone031,Clone030,Clone028,Cylinder014,Group011,Clone001005,Clone001006,Clone001010,Cylinder016,Clone002,Clone007,Clone005,Clone008,Clone009,Clone001012,Clone001013,Cylinder017,Clone001007,Clone001014,Clone001009,Clone001008,Cylinder015,Cylinder018,Cylinder020,Cylinder019,Clone001016,Clone001020,Clone001018,Clone001023,Clone001027,Cylinder021,Cylinder022,Clone001031,Clone001030,Clone001033,+181 more]
FEATURE [Part::Part2DObjectPython] Line066  # Draft 2D object (typed FeaturePython)
  ChamferSize = 0
  Closed = false
  End = (324.929,1000.03,1701.28)
  FilletRadius = 0
  Length = 1236.04
  MakeFace = true
  MapMode = 5
  Points = (2) [(1376.39,999.957,1051.5),(324.929,1000.03,1701.28)]
  Start = (1376.39,999.957,1051.5)
  Subdivisions = 0
FEATURE [Part::Part2DObjectPython] Line067  # Draft 2D object (typed FeaturePython)
  ChamferSize = 0
  Closed = false
  End = (1376.39,999.957,1051.5)
  FilletRadius = 0
  Length = 1236.04
  MakeFace = true
  MapMode = 5
  Points = (2) [(324.929,1000.03,1701.28),(1376.39,999.957,1051.5)]
  Start = (324.929,1000.03,1701.28)
  Subdivisions = 0
FEATURE [Part::Part2DObjectPython] Line068  # Draft 2D object (typed FeaturePython)
  ChamferSize = 0
  Closed = false
  End = (552.796,1701.28,894.456)
  FilletRadius = 0
  Length = 1093.08
  MakeFace = true
  MapMode = 5
  Points = (2) [(1376.39,999.957,1051.5),(552.796,1701.28,894.456)]
  Start = (1376.39,999.957,1051.5)
  Subdivisions = 0
FEATURE [Part::Part2DObjectPython] Line069  # Draft 2D object (typed FeaturePython)
  ChamferSize = 0
  Closed = false
  End = (552.796,1701.28,894.456)
  FilletRadius = 0
  Length = 1093
  MakeFace = true
  MapMode = 5
  Points = (2) [(324.929,1000.03,1701.28),(552.796,1701.28,894.456)]
  Start = (324.929,1000.03,1701.28)
  Subdivisions = 0
FEATURE [Part::Part2DObjectPython] Line070  # Draft 2D object (typed FeaturePython)
  ChamferSize = 0
  Closed = false
  End = (-525.738,1618.01,1051.5)
  FilletRadius = 0
  Length = 1093.08
  MakeFace = true
  MapMode = 5
  Points = (2) [(552.796,1701.28,894.456),(-525.738,1618.01,1051.5)]
  Start = (552.796,1701.28,894.456)
  Subdivisions = 0
FEATURE [Part::Part2DObjectPython] Line071  # Draft 2D object (typed FeaturePython)
  ChamferSize = 0
  Closed = false
  End = (324.929,1000.03,1701.28)
  FilletRadius = 0
  Length = 1236.02
  MakeFace = true
  MapMode = 5
  Points = (2) [(-525.738,1618.01,1051.5),(324.929,1000.03,1701.28)]
  Start = (-525.738,1618.01,1051.5)
  Subdivisions = 0
FEATURE [Part::Part2DObjectPython] Line072  # Draft 2D object (typed FeaturePython)
  ChamferSize = 0
  Closed = false
  End = (3.6e-11,2000,0)
  FilletRadius = 0
  Length = 1236.11
  MakeFace = true
  MapMode = 5
  Points = (2) [(-525.738,1618.01,1051.5),(3.56977e-11,2000,0)]
  Start = (-525.738,1618.01,1051.5)
  Subdivisions = 0
FEATURE [Part::Part2DObjectPython] Line073  # Draft 2D object (typed FeaturePython)
  ChamferSize = 0
  Closed = false
  End = (552.796,1701.28,894.456)
  FilletRadius = 0
  Length = 1093.1
  MakeFace = true
  MapMode = 5
  Points = (2) [(3.56977e-11,2000,0),(552.796,1701.28,894.456)]
  Start = (3.6e-11,2000,0)
  Subdivisions = 0
FEATURE [Part::Part2DObjectPython] Line074  # Draft 2D object (typed FeaturePython)
  ChamferSize = 0
  Closed = false
  End = (-525.738,1618.01,1051.5)
  FilletRadius = 0
  Length = 1093.08
  MakeFace = true
  MapMode = 5
  Points = (2) [(552.796,1701.28,894.456),(-525.738,1618.01,1051.5)]
  Start = (552.796,1701.28,894.456)
  Subdivisions = 0
FEATURE [Part::Part2DObjectPython] Line075  # Draft 2D object (typed FeaturePython)
  ChamferSize = 0
  Closed = false
  End = (1175.6,1618.02,0)
  FilletRadius = 0
  Length = 1236.11
  MakeFace = true
  MapMode = 5
  Points = (2) [(1376.39,999.957,1051.5),(1175.6,1618.02,0)]
  Start = (1376.39,999.957,1051.5)
  Subdivisions = 0
FEATURE [Part::Part2DObjectPython] Line076  # Draft 2D object (typed FeaturePython)
  ChamferSize = 0
  Closed = false
  End = (552.796,1701.28,894.456)
  FilletRadius = 0
  Length = 1093.1
  MakeFace = true
  MapMode = 5
  Points = (2) [(1175.6,1618.02,0),(552.796,1701.28,894.456)]
  Start = (1175.6,1618.02,0)
  Subdivisions = 0
FEATURE [Part::Part2DObjectPython] Line077  # Draft 2D object (typed FeaturePython)
  ChamferSize = 0
  Closed = false
  End = (-3.6e-11,2000,0)
  FilletRadius = 0
  Length = 1236.1
  MakeFace = true
  MapMode = 5
  Points = (2) [(1175.6,1618.02,0),(-3.5925e-11,2000,0)]
  Start = (1175.6,1618.02,0)
  Subdivisions = 0
FEATURE [Part::Part2DObjectPython] Line078  # Draft 2D object (typed FeaturePython)
  ChamferSize = 0
  Closed = false
  End = (1175.6,1618.02,0)
  FilletRadius = 0
  Length = 1236.1
  MakeFace = true
  MapMode = 5
  Points = (2) [(1902.16,617.998,0),(1175.6,1618.02,0)]
  Start = (1902.16,617.998,0)
  Subdivisions = 0
FEATURE [Part::Part2DObjectPython] Line079  # Draft 2D object (typed FeaturePython)
  ChamferSize = 0
  Closed = false
  End = (1788.83,-9.65e-10,894.484)
  FilletRadius = 0
  Length = 1092.97
  MakeFace = true
  MapMode = 5
  Points = (2) [(1051.49,1.3321e-09,1701.28),(1788.83,-9.64734e-10,894.484)]
  Start = (1051.49,1.332e-09,1701.28)
  Subdivisions = 0
FEATURE [Part::Part2DObjectPython] Line080  # Draft 2D object (typed FeaturePython)
  ChamferSize = 0
  Closed = false
  End = (1376.39,-999.957,1051.5)
  FilletRadius = 0
  Length = 1093.01
  MakeFace = true
  MapMode = 5
  Points = (2) [(1788.83,-9.64734e-10,894.484),(1376.39,-999.957,1051.5)]
  Start = (1788.83,-9.65e-10,894.484)
  Subdivisions = 0
FEATURE [Part::Part2DObjectPython] Line081  # Draft 2D object (typed FeaturePython)
  ChamferSize = 0
  Closed = false
  End = (1788.83,-9.65e-10,894.484)
  FilletRadius = 0
  Length = 1093.01
  MakeFace = true
  MapMode = 5
  Points = (2) [(1376.39,-999.957,1051.5),(1788.83,-9.64734e-10,894.484)]
  Start = (1376.39,-999.957,1051.5)
  Subdivisions = 0
FEATURE [Part::Part2DObjectPython] Line082  # Draft 2D object (typed FeaturePython)
  ChamferSize = 0
  Closed = false
  End = (1902.16,-617.998,0)
  FilletRadius = 0
  Length = 1093.1
  MakeFace = true
  MapMode = 5
  Points = (2) [(1788.83,-9.64734e-10,894.484),(1902.16,-617.998,0)]
  Start = (1788.83,-9.65e-10,894.484)
  Subdivisions = 0
FEATURE [Part::Part2DObjectPython] Line083  # Draft 2D object (typed FeaturePython)
  ChamferSize = 0
  Closed = false
  End = (1902.16,617.998,0)
  FilletRadius = 0
  Length = 1093.1
  MakeFace = true
  MapMode = 5
  Points = (2) [(1788.83,-9.64734e-10,894.484),(1902.16,617.998,0)]
  Start = (1788.83,-9.65e-10,894.484)
  Subdivisions = 0
FEATURE [Part::Part2DObjectPython] Line084  # Draft 2D object (typed FeaturePython)
  ChamferSize = 0
  Closed = false
  End = (1376.39,999.957,1051.5)
  FilletRadius = 0
  Length = 1093.01
  MakeFace = true
  MapMode = 5
  Points = (2) [(1788.83,-9.64734e-10,894.484),(1376.39,999.957,1051.5)]
  Start = (1788.83,-9.65e-10,894.484)
  Subdivisions = 0
FEATURE [Part::Part2DObjectPython] Line085  # Draft 2D object (typed FeaturePython)
  ChamferSize = 0
  Closed = false
  End = (-525.738,1618.01,1051.5)
  FilletRadius = 0
  Length = 1236.01
  MakeFace = true
  MapMode = 5
  Points = (2) [(-850.675,618.052,1701.28),(-525.738,1618.01,1051.5)]
  Start = (-850.675,618.052,1701.28)
  Subdivisions = 0
FEATURE [Part::Part2DObjectPython] Line086  # Draft 2D object (typed FeaturePython)
  ChamferSize = 0
  Closed = false
  End = (-1175.6,1618.02,0)
  FilletRadius = 0
  Length = 1236.11
  MakeFace = true
  MapMode = 5
  Points = (2) [(-525.738,1618.01,1051.5),(-1175.6,1618.02,0)]
  Start = (-525.738,1618.01,1051.5)
  Subdivisions = 0
FEATURE [Part::Part2DObjectPython] Line087  # Draft 2D object (typed FeaturePython)
  ChamferSize = 0
  Closed = false
  End = (-1175.6,1618.02,0)
  FilletRadius = 0
  Length = 1236.1
  MakeFace = true
  MapMode = 5
  Points = (2) [(3.56977e-11,2000,0),(-1175.6,1618.02,0)]
  Start = (3.6e-11,2000,0)
  Subdivisions = 0
FEATURE [Part::Part2DObjectPython] Line088  # Draft 2D object (typed FeaturePython)
  ChamferSize = 0
  Closed = false
  End = (-1701.28,-1.022e-09,1051.5)
  FilletRadius = 0
  Length = 1236.02
  MakeFace = true
  MapMode = 5
  Points = (2) [(-850.675,618.052,1701.28),(-1701.28,-1.02242e-09,1051.5)]
  Start = (-850.675,618.052,1701.28)
  Subdivisions = 0
FEATURE [Part::Part2DObjectPython] Line089  # Draft 2D object (typed FeaturePython)
  ChamferSize = 0
  Closed = false
  End = (-1175.6,1618.02,0)
  FilletRadius = 0
  Length = 1236.1
  MakeFace = true
  MapMode = 5
  Points = (2) [(-1902.16,617.998,0),(-1175.6,1618.02,0)]
  Start = (-1902.16,617.998,0)
  Subdivisions = 0
FEATURE [Part::Part2DObjectPython] Line090  # Draft 2D object (typed FeaturePython)
  ChamferSize = 0
  Closed = false
  End = (-1447.21,1051.46,894.426)
  FilletRadius = 0
  Length = 1093.05
  MakeFace = true
  MapMode = 5
  Points = (2) [(-525.738,1618.01,1051.5),(-1447.21,1051.46,894.426)]
  Start = (-525.738,1618.01,1051.5)
  Subdivisions = 0
FEATURE [Part::Part2DObjectPython] Line091  # Draft 2D object (typed FeaturePython)
  ChamferSize = 0
  Closed = false
  End = (-1175.6,1618.02,0)
  FilletRadius = 0
  Length = 1093.05
  MakeFace = true
  MapMode = 5
  Points = (2) [(-1447.21,1051.46,894.426),(-1175.6,1618.02,0)]
  Start = (-1447.21,1051.46,894.426)
  Subdivisions = 0
FEATURE [Part::Part2DObjectPython] Line092  # Draft 2D object (typed FeaturePython)
  ChamferSize = 0
  Closed = false
  End = (-1902.16,617.998,0)
  FilletRadius = 0
  Length = 1093.1
  MakeFace = true
  MapMode = 5
  Points = (2) [(-1447.21,1051.46,894.426),(-1902.16,617.998,0)]
  Start = (-1447.21,1051.46,894.426)
  Subdivisions = 0
FEATURE [Part::Part2DObjectPython] Line093  # Draft 2D object (typed FeaturePython)
  ChamferSize = 0
  Closed = false
  End = (-1701.28,-1.022e-09,1051.5)
  FilletRadius = 0
  Length = 1093.07
  MakeFace = true
  MapMode = 5
  Points = (2) [(-1447.21,1051.46,894.426),(-1701.28,-1.02242e-09,1051.5)]
  Start = (-1447.21,1051.46,894.426)
  Subdivisions = 0
FEATURE [Part::Part2DObjectPython] Line094  # Draft 2D object (typed FeaturePython)
  ChamferSize = 0
  Closed = false
  End = (-850.675,618.052,1701.28)
  FilletRadius = 0
  Length = 1093.03
  MakeFace = true
  MapMode = 5
  Points = (2) [(-1447.21,1051.46,894.426),(-850.675,618.052,1701.28)]
  Start = (-1447.21,1051.46,894.426)
  Subdivisions = 0
FEATURE [Part::Part2DObjectPython] Line095  # Draft 2D object (typed FeaturePython)
  ChamferSize = 0
  Closed = false
  End = (-850.675,618.052,1701.28)
  FilletRadius = 0
  Length = 1236.1
  MakeFace = true
  MapMode = 5
  Points = (2) [(324.929,1000.03,1701.28),(-850.675,618.052,1701.28)]
  Start = (324.929,1000.03,1701.28)
  Subdivisions = 0
FEATURE [Part::Part2DObjectPython] Line096  # Draft 2D object (typed FeaturePython)
  ChamferSize = 0
  Closed = false
  End = (-1902.16,617.998,0)
  FilletRadius = 0
  Length = 1236.09
  MakeFace = true
  MapMode = 5
  Points = (2) [(-1701.28,-1.02242e-09,1051.5),(-1902.16,617.998,0)]
  Start = (-1701.28,-1.022e-09,1051.5)
  Subdivisions = 0
FEATURE [Part::Part2DObjectPython] Line097  # Draft 2D object (typed FeaturePython)
  ChamferSize = 0
  Closed = false
  End = (1175.6,-1618.02,0)
  FilletRadius = 0
  Length = 1236.11
  MakeFace = true
  MapMode = 5
  Points = (2) [(1376.39,-999.957,1051.5),(1175.6,-1618.02,0)]
  Start = (1376.39,-999.957,1051.5)
  Subdivisions = 0
FEATURE [Part::Part2DObjectPython] Line098  # Draft 2D object (typed FeaturePython)
  ChamferSize = 0
  Closed = false
  End = (552.796,-1701.28,894.456)
  FilletRadius = 0
  Length = 1093.1
  MakeFace = true
  MapMode = 5
  Points = (2) [(1175.6,-1618.02,0),(552.796,-1701.28,894.456)]
  Start = (1175.6,-1618.02,0)
  Subdivisions = 0
FEATURE [Part::Part2DObjectPython] Line099  # Draft 2D object (typed FeaturePython)
  ChamferSize = 0
  Closed = false
  End = (1376.39,-999.957,1051.5)
  FilletRadius = 0
  Length = 1093.08
  MakeFace = true
  MapMode = 5
  Points = (2) [(552.796,-1701.28,894.456),(1376.39,-999.957,1051.5)]
  Start = (552.796,-1701.28,894.456)
  Subdivisions = 0
FEATURE [Part::Part2DObjectPython] Line100  # Draft 2D object (typed FeaturePython)
  ChamferSize = 0
  Closed = false
  End = (324.937,-1000.03,1701.28)
  FilletRadius = 0
  Length = 1093
  MakeFace = true
  MapMode = 5
  Points = (2) [(552.796,-1701.28,894.456),(324.937,-1000.03,1701.28)]
  Start = (552.796,-1701.28,894.456)
  Subdivisions = 0
FEATURE [Part::Part2DObjectPython] Line101  # Draft 2D object (typed FeaturePython)
  ChamferSize = 0
  Closed = false
  End = (-525.738,-1618.01,1051.5)
  FilletRadius = 0
  Length = 1236.03
  MakeFace = true
  MapMode = 5
  Points = (2) [(324.937,-1000.03,1701.28),(-525.738,-1618.01,1051.5)]
  Start = (324.937,-1000.03,1701.28)
  Subdivisions = 0
FEATURE [Part::Part2DObjectPython] Line102  # Draft 2D object (typed FeaturePython)
  ChamferSize = 0
  Closed = false
  End = (552.796,-1701.28,894.456)
  FilletRadius = 0
  Length = 1093.08
  MakeFace = true
  MapMode = 5
  Points = (2) [(-525.738,-1618.01,1051.5),(552.796,-1701.28,894.456)]
  Start = (-525.738,-1618.01,1051.5)
  Subdivisions = 0
FEATURE [Part::Part2DObjectPython] Line103  # Draft 2D object (typed FeaturePython)
  ChamferSize = 0
  Closed = false
  End = (-3.6e-11,-2000,0)
  FilletRadius = 0
  Length = 1093.1
  MakeFace = true
  MapMode = 5
  Points = (2) [(552.796,-1701.28,894.456),(-3.5925e-11,-2000,0)]
  Start = (552.796,-1701.28,894.456)
  Subdivisions = 0
FEATURE [Part::Part2DObjectPython] Line104  # Draft 2D object (typed FeaturePython)
  ChamferSize = 0
  Closed = false
  End = (1175.6,-1618.02,0)
  FilletRadius = 0
  Length = 1236.1
  MakeFace = true
  MapMode = 5
  Points = (2) [(-3.5925e-11,-2000,0),(1175.6,-1618.02,0)]
  Start = (-3.6e-11,-2000,0)
  Subdivisions = 0
FEATURE [Part::Part2DObjectPython] Line105  # Draft 2D object (typed FeaturePython)
  ChamferSize = 0
  Closed = false
  End = (-525.738,-1618.01,1051.5)
  FilletRadius = 0
  Length = 1236.11
  MakeFace = true
  MapMode = 5
  Points = (2) [(-3.5925e-11,-2000,0),(-525.738,-1618.01,1051.5)]
  Start = (-3.6e-11,-2000,0)
  Subdivisions = 0
FEATURE [Part::Part2DObjectPython] Line106  # Draft 2D object (typed FeaturePython)
  ChamferSize = 0
  Closed = false
  End = (-850.675,-618.052,1701.28)
  FilletRadius = 0
  Length = 1236.02
  MakeFace = true
  MapMode = 5
  Points = (2) [(-1701.28,-1.02242e-09,1051.5),(-850.675,-618.052,1701.28)]
  Start = (-1701.28,-1.022e-09,1051.5)
  Subdivisions = 0
FEATURE [Part::Part2DObjectPython] Line107  # Draft 2D object (typed FeaturePython)
  ChamferSize = 0
  Closed = false
  End = (-1902.16,-617.998,0)
  FilletRadius = 0
  Length = 1236.09
  MakeFace = true
  MapMode = 5
  Points = (2) [(-1701.28,-1.02242e-09,1051.5),(-1902.16,-617.998,0)]
  Start = (-1701.28,-1.022e-09,1051.5)
  Subdivisions = 0
FEATURE [Part::Part2DObjectPython] Line108  # Draft 2D object (typed FeaturePython)
  ChamferSize = 0
  Closed = false
  End = (-1902.16,617.998,0)
  FilletRadius = 0
  Length = 1236
  MakeFace = true
  MapMode = 5
  Points = (2) [(-1902.16,-617.998,0),(-1902.16,617.998,0)]
  Start = (-1902.16,-617.998,0)
  Subdivisions = 0
FEATURE [Part::Part2DObjectPython] Line109  # Draft 2D object (typed FeaturePython)
  ChamferSize = 0
  Closed = false
  End = (-525.738,-1618.01,1051.5)
  FilletRadius = 0
  Length = 1236.01
  MakeFace = true
  MapMode = 5
  Points = (2) [(-850.675,-618.052,1701.28),(-525.738,-1618.01,1051.5)]
  Start = (-850.675,-618.052,1701.28)
  Subdivisions = 0
FEATURE [Part::Part2DObjectPython] Line110  # Draft 2D object (typed FeaturePython)
  ChamferSize = 0
  Closed = false
  End = (-1175.6,-1618.02,0)
  FilletRadius = 0
  Length = 1236.11
  MakeFace = true
  MapMode = 5
  Points = (2) [(-525.738,-1618.01,1051.5),(-1175.6,-1618.02,0)]
  Start = (-525.738,-1618.01,1051.5)
  Subdivisions = 0
FEATURE [Part::Part2DObjectPython] Line111  # Draft 2D object (typed FeaturePython)
  ChamferSize = 0
  Closed = false
  End = (-1902.16,-617.998,0)
  FilletRadius = 0
  Length = 1236.1
  MakeFace = true
  MapMode = 5
  Points = (2) [(-1175.6,-1618.02,0),(-1902.16,-617.998,0)]
  Start = (-1175.6,-1618.02,0)
  Subdivisions = 0
FEATURE [Part::Part2DObjectPython] Line112  # Draft 2D object (typed FeaturePython)
  ChamferSize = 0
  Closed = false
  End = (-1447.19,-1051.45,894.481)
  FilletRadius = 0
  Length = 1093.15
  MakeFace = true
  MapMode = 5
  Points = (2) [(-1902.16,-617.998,0),(-1447.19,-1051.45,894.481)]
  Start = (-1902.16,-617.998,0)
  Subdivisions = 0
FEATURE [Part::Part2DObjectPython] Line113  # Draft 2D object (typed FeaturePython)
  ChamferSize = 0
  Closed = false
  End = (-1701.28,-1.022e-09,1051.5)
  FilletRadius = 0
  Length = 1093.05
  MakeFace = true
  MapMode = 5
  Points = (2) [(-1447.19,-1051.45,894.481),(-1701.28,-1.02242e-09,1051.5)]
  Start = (-1447.19,-1051.45,894.481)
  Subdivisions = 0
FEATURE [Part::Part2DObjectPython] Line114  # Draft 2D object (typed FeaturePython)
  ChamferSize = 0
  Closed = false
  End = (-850.675,-618.052,1701.28)
  FilletRadius = 0
  Length = 1092.97
  MakeFace = true
  MapMode = 5
  Points = (2) [(-1447.19,-1051.45,894.481),(-850.675,-618.052,1701.28)]
  Start = (-1447.19,-1051.45,894.481)
  Subdivisions = 0
FEATURE [Part::Part2DObjectPython] Line115  # Draft 2D object (typed FeaturePython)
  ChamferSize = 0
  Closed = false
  End = (-525.738,-1618.01,1051.5)
  FilletRadius = 0
  Length = 1093.03
  MakeFace = true
  MapMode = 5
  Points = (2) [(-1447.19,-1051.45,894.481),(-525.738,-1618.01,1051.5)]
  Start = (-1447.19,-1051.45,894.481)
  Subdivisions = 0
FEATURE [Part::Part2DObjectPython] Line116  # Draft 2D object (typed FeaturePython)
  ChamferSize = 0
  Closed = false
  End = (-1175.6,-1618.02,0)
  FilletRadius = 0
  Length = 1093.1
  MakeFace = true
  MapMode = 5
  Points = (2) [(-1447.19,-1051.45,894.481),(-1175.6,-1618.02,0)]
  Start = (-1447.19,-1051.45,894.481)
  Subdivisions = 0
FEATURE [Part::Part2DObjectPython] Line117  # Draft 2D object (typed FeaturePython)
  ChamferSize = 0
  Closed = false
  End = (-3.6e-11,-2000,0)
  FilletRadius = 0
  Length = 1236.1
  MakeFace = true
  MapMode = 5
  Points = (2) [(-1175.6,-1618.02,0),(-3.5925e-11,-2000,0)]
  Start = (-1175.6,-1618.02,0)
  Subdivisions = 0
FEATURE [Part::Part2DObjectPython] Line118  # Draft 2D object (typed FeaturePython)
  ChamferSize = 0
  Closed = false
  End = (-850.675,618.052,1701.28)
  FilletRadius = 0
  Length = 1093.1
  MakeFace = true
  MapMode = 5
  Points = (2) [(-1.99876e-10,3.00061e-10,2000),(-850.675,618.052,1701.28)]
  Start = (-2e-10,3e-10,2000)
  Subdivisions = 0
FEATURE [Part::Part2DObjectPython] Line119  # Draft 2D object (typed FeaturePython)
  ChamferSize = 0
  Closed = false
  End = (-850.675,-618.052,1701.28)
  FilletRadius = 0
  Length = 1093.1
  MakeFace = true
  MapMode = 5
  Points = (2) [(-1.99876e-10,3.00061e-10,2000),(-850.675,-618.052,1701.28)]
  Start = (-2e-10,3e-10,2000)
  Subdivisions = 0
FEATURE [Part::Part2DObjectPython] Line120  # Draft 2D object (typed FeaturePython)
  ChamferSize = 0
  Closed = false
  End = (324.937,-1000.03,1701.28)
  FilletRadius = 0
  Length = 1093.1
  MakeFace = true
  MapMode = 5
  Points = (2) [(-1.99876e-10,3.00061e-10,2000),(324.937,-1000.03,1701.28)]
  Start = (-2e-10,3e-10,2000)
  Subdivisions = 0
FEATURE [Part::Part2DObjectPython] Line121  # Draft 2D object (typed FeaturePython)
  ChamferSize = 0
  Closed = false
  End = (1051.49,1.332e-09,1701.28)
  FilletRadius = 0
  Length = 1093.1
  MakeFace = true
  MapMode = 5
  Points = (2) [(-1.99876e-10,3.00061e-10,2000),(1051.49,1.3321e-09,1701.28)]
  Start = (-2e-10,3e-10,2000)
  Subdivisions = 0
FEATURE [Part::Part2DObjectPython] Line122  # Draft 2D object (typed FeaturePython)
  ChamferSize = 0
  Closed = false
  End = (324.929,1000.03,1701.28)
  FilletRadius = 0
  Length = 1093.1
  MakeFace = true
  MapMode = 5
  Points = (2) [(-1.99876e-10,3.00061e-10,2000),(324.929,1000.03,1701.28)]
  Start = (-2e-10,3e-10,2000)
  Subdivisions = 0
FEATURE [App::DocumentObjectGroup] Group013  label="Domo-alambrico"
  Group = -> [Line054,Line055,Line056,Line057,Line058,Line059,Line060,Line061,Line062,Line063,Line064,Line065,Line066,Line067,Line068,Line069,Line070,Line071,Line072,Line073,Line074,Line075,Line076,Line077,Line078,Line079,Line080,Line081,Line082,Line083,Line084,Line085,Line086,Line087,Line088,Line089,Line090,Line091,Line092,Line093,Line094,Line095,Line096,Line097,Line098,Line099,Line100,Line101,Line102,Line103,+19 more]
FEATURE [App::Annotation] Text  label="Texto-Material"
  LabelText = Material
  Position = (3227.54,1318.45,0)
FEATURE [App::FeaturePython] Dimension002  # Draft dimension (typed FeaturePython)
  Dimline = (-3.6e-11,-2000,0)
  Direction = (0,0,0)
  Distance = 4000
  End = (-3.6e-11,-2000,0)
  Normal = (0,0,1)
  Start = (-3.6e-11,2000,0)
FEATURE [App::FeaturePython] Dimension003  # Draft dimension (typed FeaturePython)
  Dimline = (-2e-10,3e-10,0)
  Direction = (0,0,0)
  Distance = 2000
  End = (-2e-10,3e-10,0)
  Normal = (0,-1,0)
  Start = (-2e-10,3e-10,2000)
FEATURE [App::FeaturePython] Dimension004  # Draft dimension (typed FeaturePython)
  Dimline = (2000,-600,0)
  Direction = (0,0,0)
  Distance = 1236
  End = (1902.16,-617.998,0)
  Normal = (0,0,1)
  Start = (1902.16,617.998,0)
FEATURE [App::FeaturePython] Dimension005  # Draft dimension (typed FeaturePython)
  Dimline = (1692.93,0,1177.36)
  Direction = (0,0,0)
  Distance = 1092.97
  End = (1788.83,-9.65e-10,894.484)
  Normal = (0,-1,0)
  Start = (1051.49,1.332e-09,1701.28)
FEATURE [App::DocumentObjectGroup] Group014  label="Dimensions"
  Group = -> [Dimension002,Dimension003,Dimension004,Dimension005]
FEATURE [Part::Feature] Cylinder079  label="Varilla-B-modif-039"
  Placement = pos=(3067.05,988.83,0) rot=(1,1.4e-05,1.4e-05;1.5708rad)
  shape: bbox 10.03 x 1189 x 10 mm, 3 faces (baked)
FEATURE [Part::Feature] Cylinder081  label="Cylinder078"
  Placement = pos=(2871.13,-200,5.93e-10) rot=(-1,0,0;1.5708rad)
  shape: bbox 10 x 1047 x 10 mm, 3 faces (baked)
FEATURE [App::Annotation] Text002  label="Texto-varillas"
  LabelText = Varillas
  Position = (2851.65,1075.67,0)
FEATURE [App::Annotation] Text006  label="Texto-varilla-B"
  LabelText = B
  Position = (3045.54,-293.166,0)
FEATURE [App::Annotation] Text007  label="Texto-varilla-A"
  LabelText = A
  Position = (2839.02,-294.635,0)
FEATURE [Part::Feature] Clone001171  label="Hub5-01-clave008"
  Placement = pos=(3486.66,751.241,9.4e-14) rot=(0,0,-1;0.314151rad)
  shape: bbox 54.38 x 55.6 x 12.4 mm, 25 faces (baked)
FEATURE [Part::Feature] Clone001172  label="Hub-032"
  Placement = pos=(3822.07,752.602,-9.09e-13) rot=(0,0,1;0.523599rad)
  shape: bbox 53.16 x 55.6 x 12.4 mm, 28 faces (baked)
FEATURE [App::Annotation] Text008  label="Texto-Piezas-impresas"
  LabelText = Piezas impresas 3D
  Position = (3335.62,1068.59,0)
FEATURE [App::Annotation] Text009  label="Texto-conector-pentagonal"
  LabelText = Conector | pentagonal
  Position = (3357.25,917.695,0)
FEATURE [App::Annotation] Text010  label="Texto-conector-hexagonal"
  LabelText = Conector | Hexagonal
  Position = (3702.82,917.695,0)
FEATURE [Part::Feature] Clone001176  label="strutcap177"
  Placement = pos=(3662.75,464.083,20) rot=(1,0,0;3.14159rad)
  shape: bbox 20.3 x 20 x 30 mm, 19 faces (baked)
FEATURE [App::Annotation] Text012  label="Texto-varillas005"
  LabelText = Teton
  Position = (3595.02,530.248,0)
FEATURE [Part::Feature] Chamfer002  label="Tuerca-M3"
  Placement = pos=(3453.75,-347.288,0) rot=(1,0,0;1.5708rad)
  shape: bbox 6.35 x 6.35 x 2.4 mm, 29 faces (baked)
FEATURE [Part::Feature] Part__Feature002  label="Tornillo-M3"
  Placement = pos=(3442.59,-46.9489,3) rot=(0,-1,0;1.5708rad)
  shape: bbox 13 x 5.5 x 5.5 mm, 16 faces (baked)
FEATURE [App::Annotation] Text017  label="Texto-x30"
  LabelText = x30
  Position = (2840.67,-387.052,0)
FEATURE [App::Annotation] Text019  label="Texto-x35"
  LabelText = x35
  Position = (3032.11,-387.052,0)
FEATURE [App::Annotation] Text020
  LabelText = Tuercas M3
  Position = (3378.67,-274.428,0)
FEATURE [App::Annotation] Text021
  LabelText = Tornillos M3 x 10mm
  Position = (3372,13.5051,0)
FEATURE [App::Annotation] Text022  label="Texto-x6"
  LabelText = x6
  Position = (3441.07,635.345,0)
FEATURE [App::Annotation] Text023  label="Texto-x20"
  LabelText = x20
  Position = (3785.21,635.345,0)
FEATURE [App::Annotation] Text024  label="Texto-x037"
  LabelText = x160
  Position = (3595.42,372.947,0)
FEATURE [Part::Part2DObjectPython] Rectangle  # Draft 2D object (typed FeaturePython)
  ChamferSize = 0
  Columns = 1
  FilletRadius = 0
  Height = -869.038
  Length = 778.826
  MakeFace = false
  MapMode = 5
  Placement = pos=(3282.79,1174.01,0) rot=(0,0,1;0rad)
  Rows = 1
FEATURE [App::Annotation] Text026  label="Texto-Piezas-impresas002"
  LabelText = Tornilleria
  Position = (3493.63,154.878,0)
FEATURE [Part::Part2DObjectPython] Rectangle003  # Draft 2D object (typed FeaturePython)
  ChamferSize = 0
  Columns = 1
  FilletRadius = 0
  Height = -237.557
  Length = 1305.06
  MakeFace = false
  MapMode = 5
  Placement = pos=(2748.42,1457.07,0) rot=(0,0,1;0rad)
  Rows = 1
FEATURE [App::DocumentObjectGroup] Group017  label="Piezas-impresas"
  Group = -> [Clone001171,Clone001172,Clone001176,Text008,Text022,Text023,Text024,Rectangle,Text009,Text010,Text012]
FEATURE [App::Annotation] Text027  label="Texto-x130"
  LabelText = x130
  Position = (3503.66,-74.9347,0)
FEATURE [App::Annotation] Text028  label="Texto-x131"
  LabelText = x130
  Position = (3509.07,-372.19,0)
FEATURE [Part::Part2DObjectPython] Rectangle004  # Draft 2D object (typed FeaturePython)
  ChamferSize = 0
  Columns = 1
  FilletRadius = 0
  Height = -688.616
  Length = 787.849
  MakeFace = false
  MapMode = 5
  Placement = pos=(3285.28,239.952,0) rot=(0,0,1;0rad)
  Rows = 1
FEATURE [App::DocumentObjectGroup] Group018  label="Tornilleria"
  Group = -> [Text026,Text020,Text021,Part__Feature002,Chamfer002,Text027,Text028,Rectangle004]
FEATURE [Part::Part2DObjectPython] Rectangle005  # Draft 2D object (typed FeaturePython)
  ChamferSize = 0
  Columns = 1
  FilletRadius = 0
  Height = -1623.39
  Length = 466.45
  MakeFace = false
  MapMode = 5
  Placement = pos=(2751.78,1169.58,0) rot=(0,0,1;0rad)
  Rows = 1
FEATURE [App::DocumentObjectGroup] Group016  label="Varillas"
  Group = -> [Cylinder079,Cylinder081,Text002,Text006,Text007,Text017,Text019,Rectangle005]
FEATURE [App::DocumentObjectGroup] Group015  label="Materiales"
  Group = -> [Group016,Text,Group017,Group018,Rectangle003]
FEATURE [Part::Feature] Clone001177  label="strutcap178"
  Placement = pos=(-20,-1.7017e-11,-9.6998e-11) rot=(0.707107,0,0.707107;3.14159rad)
  shape: bbox 30 x 20 x 20.3 mm, 19 faces (baked)
FEATURE [Part::Feature] Part__Feature  label="Tornillo-M004"
  Placement = pos=(-5.55,-1.70132e-11,29.9) rot=(0,0,1;0rad)
  shape: bbox 5.5 x 5.5 x 13 mm, 16 faces (baked)
FEATURE [Part::Feature] Chamfer  label="Tuerca-M004"
  Placement = pos=(9.45,-1.7019e-11,6.96667) rot=(1,0,0;1.5708rad)
  shape: bbox 6.35 x 6.35 x 2.4 mm, 29 faces (baked)
FEATURE [Part::Feature] Cylinder082  label="Varilla-B-modif-040"
  Placement = pos=(16.0356,-0.0024909,5.5791e-06) rot=(0.57734,0.577355,0.577355;2.09441rad)
  shape: bbox 1189 x 10.03 x 10 mm, 3 faces (baked)
FEATURE [Part::Part2DObjectPython] Line124  # Draft 2D object (typed FeaturePython)
  ChamferSize = 0
  Closed = false
  End = (-5.55,-1.7e-11,6.56667)
  FilletRadius = 0
  Length = 2.8
  MakeFace = true
  MapMode = 5
  Points = (2) [(-5.55,-1.70175e-11,9.36667),(-5.55,-1.70176e-11,6.56667)]
  Start = (-5.55,-1.7e-11,9.36667)
  Subdivisions = 0
  Support = -> [Clone001177]
FEATURE [Part::Part2DObjectPython] Line125  # Draft 2D object (typed FeaturePython)
  ChamferSize = 0
  Closed = false
  End = (6.7,-1.7e-11,8.16667)
  FilletRadius = 0
  Length = 12.2516
  MakeFace = true
  MapMode = 5
  Points = (2) [(-5.55,-1.70176e-11,7.96667),(6.7,-1.70192e-11,8.16667)]
  Start = (-5.55,-1.7e-11,7.96667)
  Subdivisions = 0
FEATURE [Part::Part2DObjectPython] Line126  # Draft 2D object (typed FeaturePython)
  ChamferSize = 0
  Closed = false
  End = (-5.55,-1.7e-11,7.96667)
  FilletRadius = 0
  Length = 11.9333
  MakeFace = true
  MapMode = 5
  Points = (2) [(-5.55,-1.70177e-11,19.9),(-5.55,-1.70176e-11,7.96667)]
  Start = (-5.55,-1.7e-11,19.9)
  Subdivisions = 0
FEATURE [Part::Part2DObjectPython] Line127  # Draft 2D object (typed FeaturePython)
  ChamferSize = 0
  Closed = false
  End = (-5.55,-1.7e-11,6.56667)
  FilletRadius = 0
  Length = 1.6
  MakeFace = true
  MapMode = 5
  Points = (2) [(-5.55,-1.6,6.56667),(-5.55,-1.70176e-11,6.56667)]
  Start = (-5.55,-1.6,6.56667)
  Subdivisions = 0
FEATURE [App::DocumentObjectGroup] Group020  label="Despiece"
  Group = -> [Clone001177,Part__Feature,Chamfer,Cylinder082,Line124,Line125,Line126,Line127]
FEATURE [Part::Feature] Clone001178  label="strutcap179"
  Placement = pos=(-20,31.6617,-9.6998e-11) rot=(0.707107,0,0.707107;3.14159rad)
  shape: bbox 30 x 20 x 20.3 mm, 19 faces (baked)
FEATURE [Part::Feature] Part__Feature003  label="Tornillo-M005"
  Placement = pos=(-5.55,31.6617,11.9) rot=(0,0,1;0rad)
  shape: bbox 5.5 x 5.5 x 13 mm, 16 faces (baked)
FEATURE [Part::Feature] Chamfer003  label="Tuerca-M005"
  Placement = pos=(-5.55,31.6617,6.96667) rot=(1,0,0;1.5708rad)
  shape: bbox 6.35 x 6.35 x 2.4 mm, 29 faces (baked)
FEATURE [Part::Feature] Cylinder083  label="Varilla-B-modif-041"
  Placement = pos=(-20,31.6617,5.5791e-06) rot=(0.57734,0.577355,0.577355;2.09441rad)
  shape: bbox 1189 x 10.03 x 10 mm, 3 faces (baked)
FEATURE [App::DocumentObjectGroup] Group021  label="Ensamblaje"
  Group = -> [Clone001178,Part__Feature003,Chamfer003,Cylinder083]
FEATURE [App::DocumentObjectGroup] Group019  label="Ensamblaje-tetones"
  Group = -> [Group020,Group021]
